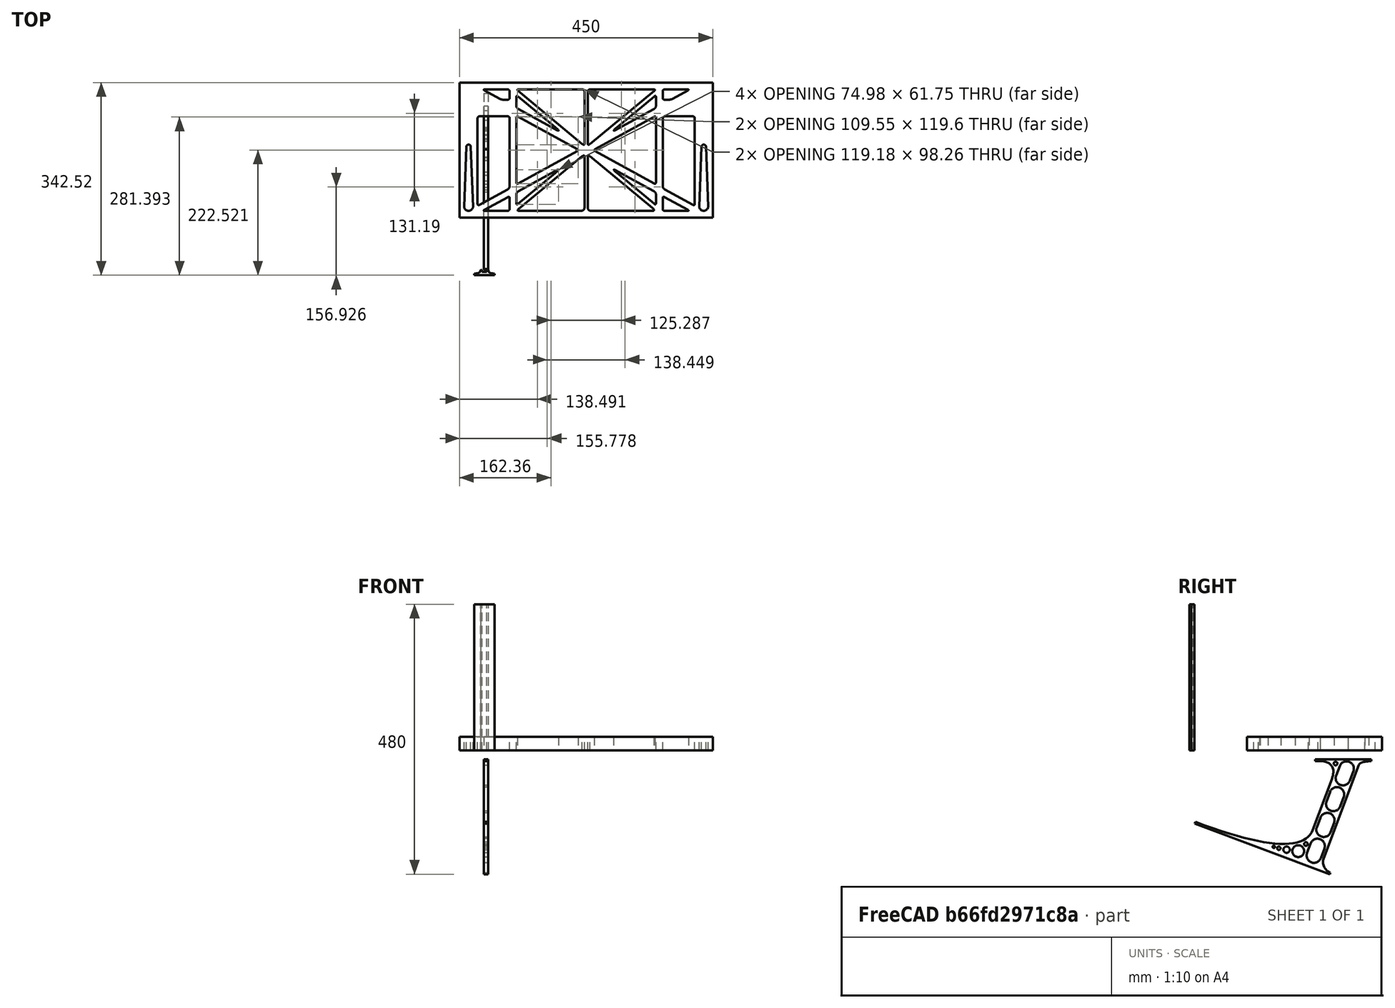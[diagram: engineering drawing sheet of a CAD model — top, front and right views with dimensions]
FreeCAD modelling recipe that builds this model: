
FCSTD DOCUMENT  (FreeCAD 0.19R0.19.2)
Label: laptopStand155FCStd
License: All rights reserved
LicenseURL: http://en.wikipedia.org/wiki/All_rights_reserved
objects: Sketcher::SketchObject×4, Part::Extrusion×3
note: 7 computed .brp shape members not serialized (recipe doc carries the construction recipe); baked Part::Feature solids carry a one-line shape summary decoded from their .brp

FEATURE [Sketcher::SketchObject] Sketch
  FullyConstrained = false
  sketch-geometry (349):
    g0: LineSegment StartX=-10.9272 StartY=-82.7794 StartZ=0 EndX=46.0728 EndY=-51.4823 EndZ=0
    g1: LineSegment StartX=-10.9272 StartY=76.4095 StartZ=0 EndX=-10.9272 EndY=-82.7794 EndZ=0
    g2: LineSegment StartX=46.0728 StartY=76.4095 StartZ=0 EndX=46.0728 EndY=-51.4823 EndZ=0
    g3: LineSegment StartX=-42.9272 StartY=136.221 StartZ=0 EndX=-42.9272 EndY=-103.779 EndZ=0
    g4: LineSegment StartX=407.073 StartY=136.221 StartZ=0 EndX=407.073 EndY=-103.779 EndZ=0
    g5: ArcOfCircle CenterX=-26.9272 CenterY=-83.7794 CenterZ=0 NormalX=0 NormalY=0 NormalZ=1 AngleXU=0 Radius=8 StartAngle=3.14159 EndAngle=6.28319
    g6: ArcOfCircle CenterX=391.073 CenterY=22.1087 CenterZ=0 NormalX=0 NormalY=0 NormalZ=1 AngleXU=0 Radius=8 StartAngle=-4.4e-15 EndAngle=3.14159
    g7: LineSegment StartX=399.073 StartY=22.1087 StartZ=0 EndX=399.073 EndY=-83.7794 EndZ=0
    g8: LineSegment StartX=383.073 StartY=22.1087 StartZ=0 EndX=383.073 EndY=-83.7794 EndZ=0
    g9: ArcOfCircle CenterX=391.073 CenterY=-83.7794 CenterZ=0 NormalX=0 NormalY=0 NormalZ=1 AngleXU=0 Radius=8 StartAngle=3.14159 EndAngle=6.28319
    g10: Circle CenterX=175.022 CenterY=27.0628 CenterZ=0 NormalX=0 NormalY=0 NormalZ=1 AngleXU=0 Radius=1
    g11: Circle CenterX=179.022 CenterY=24.8665 CenterZ=0 NormalX=0 NormalY=0 NormalZ=1 AngleXU=0 Radius=1
    g12: Circle CenterX=179.022 CenterY=27.0628 CenterZ=0 NormalX=0 NormalY=0 NormalZ=1 AngleXU=0 Radius=1
    g13: BSplineCurve PolesCount=3 KnotsCount=2 Degree=2 IsPeriodic=0
    g14: GeomPoint X=175.022 Y=27.0628 Z=0
    g15: GeomPoint X=179.022 Y=27.0628 Z=0
    g16: Circle CenterX=189.124 CenterY=27.0628 CenterZ=0 NormalX=0 NormalY=0 NormalZ=1 AngleXU=0 Radius=1
    g17: Circle CenterX=185.124 CenterY=24.8665 CenterZ=0 NormalX=0 NormalY=0 NormalZ=1 AngleXU=0 Radius=1
    g18: Circle CenterX=185.124 CenterY=27.0628 CenterZ=0 NormalX=0 NormalY=0 NormalZ=1 AngleXU=0 Radius=1
    g19: BSplineCurve PolesCount=3 KnotsCount=2 Degree=2 IsPeriodic=0
    g20: GeomPoint X=189.124 Y=27.0628 Z=0
    g21: GeomPoint X=185.124 Y=27.0628 Z=0
    g22: Circle CenterX=175.022 CenterY=5.37834 CenterZ=0 NormalX=0 NormalY=0 NormalZ=1 AngleXU=0 Radius=1
    g23: Circle CenterX=179.022 CenterY=7.57463 CenterZ=0 NormalX=0 NormalY=0 NormalZ=1 AngleXU=0 Radius=1
    g24: Circle CenterX=179.022 CenterY=5.34704 CenterZ=0 NormalX=0 NormalY=0 NormalZ=1 AngleXU=0 Radius=1
    g25: BSplineCurve PolesCount=3 KnotsCount=2 Degree=2 IsPeriodic=0
    g26: GeomPoint X=175.022 Y=5.37834 Z=0
    g27: GeomPoint X=179.022 Y=5.34704 Z=0
    g28: Circle CenterX=189.124 CenterY=5.37834 CenterZ=0 NormalX=0 NormalY=0 NormalZ=1 AngleXU=0 Radius=1
    g29: Circle CenterX=185.124 CenterY=7.57463 CenterZ=0 NormalX=0 NormalY=0 NormalZ=1 AngleXU=0 Radius=1
    g30: Circle CenterX=185.124 CenterY=5.34704 CenterZ=0 NormalX=0 NormalY=0 NormalZ=1 AngleXU=0 Radius=1
    g31: BSplineCurve PolesCount=3 KnotsCount=2 Degree=2 IsPeriodic=0
    g32: GeomPoint X=189.124 Y=5.37834 Z=0
    g33: GeomPoint X=185.124 Y=5.34704 Z=0
    g34: Circle CenterX=165.871 CenterY=18.1458 CenterZ=0 NormalX=0 NormalY=0 NormalZ=1 AngleXU=0 Radius=1
    g35: Circle CenterX=169.377 CenterY=16.2206 CenterZ=0 NormalX=0 NormalY=0 NormalZ=1 AngleXU=0 Radius=1
    g36: Circle CenterX=165.871 CenterY=14.2954 CenterZ=0 NormalX=0 NormalY=0 NormalZ=1 AngleXU=0 Radius=1
    g37: BSplineCurve PolesCount=3 KnotsCount=2 Degree=2 IsPeriodic=0
    g38: GeomPoint X=165.871 Y=18.1458 Z=0
    g39: GeomPoint X=165.871 Y=14.2954 Z=0
    g40: Circle CenterX=198.275 CenterY=18.1458 CenterZ=0 NormalX=0 NormalY=0 NormalZ=1 AngleXU=0 Radius=1
    g41: Circle CenterX=194.768 CenterY=16.2206 CenterZ=0 NormalX=0 NormalY=0 NormalZ=1 AngleXU=0 Radius=1
    g42: Circle CenterX=198.275 CenterY=14.2954 CenterZ=0 NormalX=0 NormalY=0 NormalZ=1 AngleXU=0 Radius=1
    g43: BSplineCurve PolesCount=3 KnotsCount=2 Degree=2 IsPeriodic=0
    g44: GeomPoint X=198.275 Y=18.1458 Z=0
    g45: GeomPoint X=198.275 Y=14.2954 Z=0
    g46: LineSegment StartX=407.073 StartY=-103.779 StartZ=0 EndX=-42.9272 EndY=-103.779 EndZ=0
    g47: LineSegment StartX=407.073 StartY=136.221 StartZ=0 EndX=-42.9272 EndY=136.221 EndZ=0
    g48: LineSegment StartX=46.0728 StartY=76.4095 StartZ=0 EndX=-10.9272 EndY=76.4095 EndZ=0
    g49: Circle CenterX=125.607 CenterY=54.1951 CenterZ=0 NormalX=0 NormalY=0 NormalZ=1 AngleXU=0 Radius=1
    g50: Circle CenterX=139.632 CenterY=46.4944 CenterZ=0 NormalX=0 NormalY=0 NormalZ=1 AngleXU=0 Radius=1
    g51: Circle CenterX=127.326 CenterY=56.7187 CenterZ=0 NormalX=0 NormalY=0 NormalZ=1 AngleXU=0 Radius=1
    g52: BSplineCurve PolesCount=3 KnotsCount=2 Degree=2 IsPeriodic=0
    g53: GeomPoint X=125.607 Y=54.1951 Z=0
    g54: GeomPoint X=127.326 Y=56.7187 Z=0
    g55: Circle CenterX=236.821 CenterY=56.7187 CenterZ=0 NormalX=0 NormalY=0 NormalZ=1 AngleXU=0 Radius=1
    g56: Circle CenterX=224.513 CenterY=46.4944 CenterZ=0 NormalX=0 NormalY=0 NormalZ=1 AngleXU=0 Radius=1
    g57: Circle CenterX=238.538 CenterY=54.1951 CenterZ=0 NormalX=0 NormalY=0 NormalZ=1 AngleXU=0 Radius=1
    g58: BSplineCurve PolesCount=3 KnotsCount=2 Degree=2 IsPeriodic=0
    g59: GeomPoint X=236.821 Y=56.7187 Z=0
    g60: GeomPoint X=238.538 Y=54.1951 Z=0
    g61: Circle CenterX=238.538 CenterY=-21.7539 CenterZ=0 NormalX=0 NormalY=0 NormalZ=1 AngleXU=0 Radius=1
    g62: Circle CenterX=224.513 CenterY=-14.0532 CenterZ=0 NormalX=0 NormalY=0 NormalZ=1 AngleXU=0 Radius=1
    g63: Circle CenterX=236.821 CenterY=-24.2775 CenterZ=0 NormalX=0 NormalY=0 NormalZ=1 AngleXU=0 Radius=1
    g64: BSplineCurve PolesCount=3 KnotsCount=2 Degree=2 IsPeriodic=0
    g65: GeomPoint X=238.538 Y=-21.7539 Z=0
    g66: GeomPoint X=236.821 Y=-24.2775 Z=0
    g67: Circle CenterX=125.607 CenterY=-21.7539 CenterZ=0 NormalX=0 NormalY=0 NormalZ=1 AngleXU=0 Radius=1
    g68: Circle CenterX=139.632 CenterY=-14.0532 CenterZ=0 NormalX=0 NormalY=0 NormalZ=1 AngleXU=0 Radius=1
    g69: Circle CenterX=127.325 CenterY=-24.2775 CenterZ=0 NormalX=0 NormalY=0 NormalZ=1 AngleXU=0 Radius=1
    g70: BSplineCurve PolesCount=3 KnotsCount=2 Degree=2 IsPeriodic=0
    g71: GeomPoint X=125.607 Y=-21.7539 Z=0
    g72: GeomPoint X=127.325 Y=-24.2775 Z=0
    g73: Circle CenterX=302.996 CenterY=111.695 CenterZ=0 NormalX=0 NormalY=0 NormalZ=1 AngleXU=0 Radius=1
    g74: Circle CenterX=306.073 CenterY=114.251 CenterZ=0 NormalX=0 NormalY=0 NormalZ=1 AngleXU=0 Radius=1
    g75: Circle CenterX=306.073 CenterY=110.251 CenterZ=0 NormalX=0 NormalY=0 NormalZ=1 AngleXU=0 Radius=1
    g76: BSplineCurve PolesCount=3 KnotsCount=2 Degree=2 IsPeriodic=0
    g77: GeomPoint X=302.996 Y=111.695 Z=0
    g78: GeomPoint X=306.073 Y=110.251 Z=0
    g79: Circle CenterX=306.073 CenterY=95.2763 CenterZ=0 NormalX=0 NormalY=0 NormalZ=1 AngleXU=0 Radius=1
    g80: Circle CenterX=306.073 CenterY=91.2763 CenterZ=0 NormalX=0 NormalY=0 NormalZ=1 AngleXU=0 Radius=1
    g81: Circle CenterX=302.567 CenterY=89.3511 CenterZ=0 NormalX=0 NormalY=0 NormalZ=1 AngleXU=0 Radius=1
    g82: BSplineCurve PolesCount=3 KnotsCount=2 Degree=2 IsPeriodic=0
    g83: GeomPoint X=306.073 Y=95.2763 Z=0
    g84: GeomPoint X=302.567 Y=89.3511 Z=0
    g85: LineSegment StartX=306.073 StartY=110.251 StartZ=0 EndX=306.073 EndY=95.2763 EndZ=0
    g86: LineSegment StartX=302.996 StartY=111.695 StartZ=0 EndX=236.821 EndY=56.7187 EndZ=0
    g87: LineSegment StartX=238.538 StartY=54.1951 StartZ=0 EndX=302.567 EndY=89.3511 EndZ=0
    g88: Circle CenterX=61.1496 CenterY=111.695 CenterZ=0 NormalX=0 NormalY=0 NormalZ=1 AngleXU=0 Radius=1
    g89: Circle CenterX=58.0728 CenterY=114.251 CenterZ=0 NormalX=0 NormalY=0 NormalZ=1 AngleXU=0 Radius=1
    g90: Circle CenterX=58.0728 CenterY=110.251 CenterZ=0 NormalX=0 NormalY=0 NormalZ=1 AngleXU=0 Radius=1
    g91: BSplineCurve PolesCount=3 KnotsCount=2 Degree=2 IsPeriodic=0
    g92: GeomPoint X=61.1496 Y=111.695 Z=0
    g93: GeomPoint X=58.0728 Y=110.251 Z=0
    g94: Circle CenterX=61.5791 CenterY=89.3511 CenterZ=0 NormalX=0 NormalY=0 NormalZ=1 AngleXU=0 Radius=1
    g95: Circle CenterX=58.0728 CenterY=91.2763 CenterZ=0 NormalX=0 NormalY=0 NormalZ=1 AngleXU=0 Radius=1
    g96: Circle CenterX=58.0728 CenterY=95.2763 CenterZ=0 NormalX=0 NormalY=0 NormalZ=1 AngleXU=0 Radius=1
    g97: BSplineCurve PolesCount=3 KnotsCount=2 Degree=2 IsPeriodic=0
    g98: GeomPoint X=61.5791 Y=89.3511 Z=0
    g99: GeomPoint X=58.0728 Y=95.2763 Z=0
    g100: LineSegment StartX=58.0728 StartY=110.251 StartZ=0 EndX=58.0728 EndY=95.2763 EndZ=0
    g101: LineSegment StartX=61.1496 StartY=111.695 StartZ=0 EndX=127.326 EndY=56.7187 EndZ=0
    g102: LineSegment StartX=125.607 StartY=54.1951 StartZ=0 EndX=61.5791 EndY=89.3511 EndZ=0
    g103: Circle CenterX=61.5791 CenterY=-56.9099 CenterZ=0 NormalX=0 NormalY=0 NormalZ=1 AngleXU=0 Radius=1
    g104: Circle CenterX=58.0728 CenterY=-58.8351 CenterZ=0 NormalX=0 NormalY=0 NormalZ=1 AngleXU=0 Radius=1
    g105: Circle CenterX=58.0728 CenterY=-62.8351 CenterZ=0 NormalX=0 NormalY=0 NormalZ=1 AngleXU=0 Radius=1
    g106: BSplineCurve PolesCount=3 KnotsCount=2 Degree=2 IsPeriodic=0
    g107: GeomPoint X=61.5791 Y=-56.9099 Z=0
    g108: GeomPoint X=58.0728 Y=-62.8351 Z=0
    g109: Circle CenterX=58.0728 CenterY=-77.8102 CenterZ=0 NormalX=0 NormalY=0 NormalZ=1 AngleXU=0 Radius=1
    g110: Circle CenterX=58.0728 CenterY=-81.8102 CenterZ=0 NormalX=0 NormalY=0 NormalZ=1 AngleXU=0 Radius=1
    g111: Circle CenterX=61.1496 CenterY=-79.2541 CenterZ=0 NormalX=0 NormalY=0 NormalZ=1 AngleXU=0 Radius=1
    g112: BSplineCurve PolesCount=3 KnotsCount=2 Degree=2 IsPeriodic=0
    g113: GeomPoint X=58.0728 Y=-77.8102 Z=0
    g114: GeomPoint X=61.1496 Y=-79.2541 Z=0
    g115: LineSegment StartX=58.0728 StartY=-62.8351 StartZ=0 EndX=58.0728 EndY=-77.8102 EndZ=0
    g116: LineSegment StartX=61.1496 StartY=-79.2541 StartZ=0 EndX=127.325 EndY=-24.2775 EndZ=0
    g117: LineSegment StartX=125.607 StartY=-21.7539 StartZ=0 EndX=61.5791 EndY=-56.9099 EndZ=0
    g118: Circle CenterX=302.567 CenterY=-56.9099 CenterZ=0 NormalX=0 NormalY=0 NormalZ=1 AngleXU=0 Radius=1
    g119: Circle CenterX=306.073 CenterY=-58.8351 CenterZ=0 NormalX=0 NormalY=0 NormalZ=1 AngleXU=0 Radius=1
    g120: Circle CenterX=306.073 CenterY=-62.8351 CenterZ=0 NormalX=0 NormalY=0 NormalZ=1 AngleXU=0 Radius=1
    g121: BSplineCurve PolesCount=3 KnotsCount=2 Degree=2 IsPeriodic=0
    g122: GeomPoint X=302.567 Y=-56.9099 Z=0
    g123: GeomPoint X=306.073 Y=-62.8351 Z=0
    g124: Circle CenterX=302.996 CenterY=-79.2541 CenterZ=0 NormalX=0 NormalY=0 NormalZ=1 AngleXU=0 Radius=1
    g125: Circle CenterX=306.073 CenterY=-81.8102 CenterZ=0 NormalX=0 NormalY=0 NormalZ=1 AngleXU=0 Radius=1
    g126: Circle CenterX=306.073 CenterY=-77.8102 CenterZ=0 NormalX=0 NormalY=0 NormalZ=1 AngleXU=0 Radius=1
    g127: BSplineCurve PolesCount=3 KnotsCount=2 Degree=2 IsPeriodic=0
    g128: GeomPoint X=302.996 Y=-79.2541 Z=0
    g129: GeomPoint X=306.073 Y=-77.8102 Z=0
    g130: LineSegment StartX=306.073 StartY=-62.8351 StartZ=0 EndX=306.073 EndY=-77.8102 EndZ=0
    g131: LineSegment StartX=302.996 StartY=-79.2541 StartZ=0 EndX=236.821 EndY=-24.2775 EndZ=0
    g132: LineSegment StartX=238.538 StartY=-21.7539 StartZ=0 EndX=302.567 EndY=-56.9099 EndZ=0
    g133: Circle CenterX=61.6457 CenterY=-88.8112 CenterZ=0 NormalX=0 NormalY=0 NormalZ=1 AngleXU=0 Radius=1
    g134: Circle CenterX=58.0728 CenterY=-91.7794 CenterZ=0 NormalX=0 NormalY=0 NormalZ=1 AngleXU=0 Radius=1
    g135: Circle CenterX=63.9135 CenterY=-91.7794 CenterZ=0 NormalX=0 NormalY=0 NormalZ=1 AngleXU=0 Radius=1
    g136: BSplineCurve PolesCount=3 KnotsCount=2 Degree=2 IsPeriodic=0
    g137: GeomPoint X=61.6457 Y=-88.8112 Z=0
    g138: GeomPoint X=63.9135 Y=-91.7794 Z=0
    g139: Circle CenterX=179.022 CenterY=-85.8163 CenterZ=0 NormalX=0 NormalY=0 NormalZ=1 AngleXU=0 Radius=1
    g140: Circle CenterX=179.022 CenterY=-91.7794 CenterZ=0 NormalX=0 NormalY=0 NormalZ=1 AngleXU=0 Radius=1
    g141: Circle CenterX=171.895 CenterY=-91.7794 CenterZ=0 NormalX=0 NormalY=0 NormalZ=1 AngleXU=0 Radius=1
    g142: BSplineCurve PolesCount=3 KnotsCount=2 Degree=2 IsPeriodic=0
    g143: GeomPoint X=179.022 Y=-85.8163 Z=0
    g144: GeomPoint X=171.895 Y=-91.7794 Z=0
    g145: Circle CenterX=185.124 CenterY=-86.2028 CenterZ=0 NormalX=0 NormalY=0 NormalZ=1 AngleXU=0 Radius=1
    g146: Circle CenterX=185.124 CenterY=-91.7794 CenterZ=0 NormalX=0 NormalY=0 NormalZ=1 AngleXU=0 Radius=1
    g147: Circle CenterX=191.747 CenterY=-91.7794 CenterZ=0 NormalX=0 NormalY=0 NormalZ=1 AngleXU=0 Radius=1
    g148: BSplineCurve PolesCount=3 KnotsCount=2 Degree=2 IsPeriodic=0
    g149: GeomPoint X=185.124 Y=-86.2028 Z=0
    g150: GeomPoint X=191.747 Y=-91.7794 Z=0
    g151: Circle CenterX=299.888 CenterY=-86.6413 CenterZ=0 NormalX=0 NormalY=0 NormalZ=1 AngleXU=0 Radius=1
    g152: Circle CenterX=306.073 CenterY=-91.7794 CenterZ=0 NormalX=0 NormalY=0 NormalZ=1 AngleXU=0 Radius=1
    g153: Circle CenterX=298.776 CenterY=-91.7794 CenterZ=0 NormalX=0 NormalY=0 NormalZ=1 AngleXU=0 Radius=1
    g154: BSplineCurve PolesCount=3 KnotsCount=2 Degree=2 IsPeriodic=0
    g155: GeomPoint X=299.888 Y=-86.6413 Z=0
    g156: GeomPoint X=298.776 Y=-91.7794 Z=0
    g157: LineSegment StartX=189.124 StartY=5.37834 StartZ=0 EndX=299.888 EndY=-86.6413 EndZ=0
    g158: LineSegment StartX=298.776 StartY=-91.7794 StartZ=0 EndX=191.747 EndY=-91.7794 EndZ=0
    g159: LineSegment StartX=185.124 StartY=-86.2028 StartZ=0 EndX=185.124 EndY=5.34704 EndZ=0
    g160: LineSegment StartX=179.022 StartY=5.34704 StartZ=0 EndX=179.022 EndY=-85.8163 EndZ=0
    g161: LineSegment StartX=171.895 StartY=-91.7794 StartZ=0 EndX=63.9135 EndY=-91.7794 EndZ=0
    g162: LineSegment StartX=61.6457 StartY=-88.8112 StartZ=0 EndX=175.022 EndY=5.37834 EndZ=0
    g163: Circle CenterX=302.073 CenterY=124.221 CenterZ=0 NormalX=0 NormalY=0 NormalZ=1 AngleXU=0 Radius=1
    g164: Circle CenterX=306.073 CenterY=124.221 CenterZ=0 NormalX=0 NormalY=0 NormalZ=1 AngleXU=0 Radius=1
    g165: Circle CenterX=302.996 CenterY=121.665 CenterZ=0 NormalX=0 NormalY=0 NormalZ=1 AngleXU=0 Radius=1
    g166: BSplineCurve PolesCount=3 KnotsCount=2 Degree=2 IsPeriodic=0
    g167: GeomPoint X=302.073 Y=124.221 Z=0
    g168: GeomPoint X=302.996 Y=121.665 Z=0
    g169: Circle CenterX=189.124 CenterY=124.221 CenterZ=0 NormalX=0 NormalY=0 NormalZ=1 AngleXU=0 Radius=1
    g170: Circle CenterX=185.124 CenterY=124.221 CenterZ=0 NormalX=0 NormalY=0 NormalZ=1 AngleXU=0 Radius=1
    g171: Circle CenterX=185.124 CenterY=120.221 CenterZ=0 NormalX=0 NormalY=0 NormalZ=1 AngleXU=0 Radius=1
    g172: BSplineCurve PolesCount=3 KnotsCount=2 Degree=2 IsPeriodic=0
    g173: GeomPoint X=189.124 Y=124.221 Z=0
    g174: GeomPoint X=185.124 Y=120.221 Z=0
    g175: Circle CenterX=175.022 CenterY=124.221 CenterZ=0 NormalX=0 NormalY=0 NormalZ=1 AngleXU=0 Radius=1
    g176: Circle CenterX=179.022 CenterY=124.221 CenterZ=0 NormalX=0 NormalY=0 NormalZ=1 AngleXU=0 Radius=1
    g177: Circle CenterX=179.022 CenterY=120.221 CenterZ=0 NormalX=0 NormalY=0 NormalZ=1 AngleXU=0 Radius=1
    g178: BSplineCurve PolesCount=3 KnotsCount=2 Degree=2 IsPeriodic=0
    g179: GeomPoint X=175.022 Y=124.221 Z=0
    g180: GeomPoint X=179.022 Y=120.221 Z=0
    g181: Circle CenterX=62.0728 CenterY=124.221 CenterZ=0 NormalX=0 NormalY=0 NormalZ=1 AngleXU=0 Radius=1
    g182: Circle CenterX=58.0728 CenterY=124.221 CenterZ=0 NormalX=0 NormalY=0 NormalZ=1 AngleXU=0 Radius=1
    g183: Circle CenterX=61.1496 CenterY=121.665 CenterZ=0 NormalX=0 NormalY=0 NormalZ=1 AngleXU=0 Radius=1
    g184: BSplineCurve PolesCount=3 KnotsCount=2 Degree=2 IsPeriodic=0
    g185: GeomPoint X=62.0728 Y=124.221 Z=0
    g186: GeomPoint X=61.1496 Y=121.665 Z=0
    g187: LineSegment StartX=62.0728 StartY=124.221 StartZ=0 EndX=175.022 EndY=124.221 EndZ=0
    g188: LineSegment StartX=179.022 StartY=120.221 StartZ=0 EndX=179.022 EndY=27.0628 EndZ=0
    g189: LineSegment StartX=185.124 StartY=27.0628 StartZ=0 EndX=185.124 EndY=120.221 EndZ=0
    g190: LineSegment StartX=189.124 StartY=124.221 StartZ=0 EndX=302.073 EndY=124.221 EndZ=0
    g191: LineSegment StartX=302.996 StartY=121.665 StartZ=0 EndX=189.124 EndY=27.0628 EndZ=0
    g192: LineSegment StartX=175.022 StartY=27.0628 StartZ=0 EndX=61.1496 EndY=121.665 EndZ=0
    g193: Circle CenterX=61.5791 CenterY=75.4095 CenterZ=0 NormalX=0 NormalY=0 NormalZ=1 AngleXU=0 Radius=1
    g194: Circle CenterX=58.0728 CenterY=77.3346 CenterZ=0 NormalX=0 NormalY=0 NormalZ=1 AngleXU=0 Radius=1
    g195: Circle CenterX=58.0728 CenterY=73.3346 CenterZ=0 NormalX=0 NormalY=0 NormalZ=1 AngleXU=0 Radius=1
    g196: BSplineCurve PolesCount=3 KnotsCount=2 Degree=2 IsPeriodic=0
    g197: GeomPoint X=61.5791 Y=75.4095 Z=0
    g198: GeomPoint X=58.0728 Y=73.3346 Z=0
    g199: Circle CenterX=58.0728 CenterY=-40.8935 CenterZ=0 NormalX=0 NormalY=0 NormalZ=1 AngleXU=0 Radius=1
    g200: Circle CenterX=58.0728 CenterY=-44.8935 CenterZ=0 NormalX=0 NormalY=0 NormalZ=1 AngleXU=0 Radius=1
    g201: Circle CenterX=61.5791 CenterY=-42.9683 CenterZ=0 NormalX=0 NormalY=0 NormalZ=1 AngleXU=0 Radius=1
    g202: BSplineCurve PolesCount=3 KnotsCount=2 Degree=2 IsPeriodic=0
    g203: GeomPoint X=58.0728 Y=-40.8935 Z=0
    g204: GeomPoint X=61.5791 Y=-42.9683 Z=0
    g205: LineSegment StartX=61.5791 StartY=-42.9683 StartZ=0 EndX=165.871 EndY=14.2954 EndZ=0
    g206: LineSegment StartX=165.871 StartY=18.1458 StartZ=0 EndX=61.5791 EndY=75.4095 EndZ=0
    g207: LineSegment StartX=58.0728 StartY=73.3346 StartZ=0 EndX=58.0728 EndY=-40.8935 EndZ=0
    g208: Circle CenterX=302.567 CenterY=-42.9683 CenterZ=0 NormalX=0 NormalY=0 NormalZ=1 AngleXU=0 Radius=1
    g209: Circle CenterX=306.073 CenterY=-44.8935 CenterZ=0 NormalX=0 NormalY=0 NormalZ=1 AngleXU=0 Radius=1
    g210: Circle CenterX=306.073 CenterY=-40.8935 CenterZ=0 NormalX=0 NormalY=0 NormalZ=1 AngleXU=0 Radius=1
    g211: BSplineCurve PolesCount=3 KnotsCount=2 Degree=2 IsPeriodic=0
    g212: GeomPoint X=302.567 Y=-42.9683 Z=0
    g213: GeomPoint X=306.073 Y=-40.8935 Z=0
    g214: Circle CenterX=306.073 CenterY=73.3346 CenterZ=0 NormalX=0 NormalY=0 NormalZ=1 AngleXU=0 Radius=1
    g215: Circle CenterX=306.073 CenterY=77.3346 CenterZ=0 NormalX=0 NormalY=0 NormalZ=1 AngleXU=0 Radius=1
    g216: Circle CenterX=302.567 CenterY=75.4095 CenterZ=0 NormalX=0 NormalY=0 NormalZ=1 AngleXU=0 Radius=1
    g217: BSplineCurve PolesCount=3 KnotsCount=2 Degree=2 IsPeriodic=0
    g218: GeomPoint X=306.073 Y=73.3346 Z=0
    g219: GeomPoint X=302.567 Y=75.4095 Z=0
    g220: LineSegment StartX=302.567 StartY=-42.9683 StartZ=0 EndX=198.275 EndY=14.2954 EndZ=0
    g221: LineSegment StartX=198.275 StartY=18.1458 StartZ=0 EndX=302.567 EndY=75.4095 EndZ=0
    g222: LineSegment StartX=306.073 StartY=73.3346 StartZ=0 EndX=306.073 EndY=-40.8935 EndZ=0
    g223: LineSegment StartX=322.073 StartY=105.865 StartZ=0 EndX=328.643 EndY=105.865 EndZ=0
    g224: LineSegment StartX=318.073 StartY=120.221 StartZ=0 EndX=318.073 EndY=109.865 EndZ=0
    g225: LineSegment StartX=336.157 StartY=107.779 StartZ=0 EndX=362.567 EndY=122.294 EndZ=0
    g226: Circle CenterX=362.073 CenterY=124.221 CenterZ=0 NormalX=0 NormalY=0 NormalZ=1 AngleXU=0 Radius=1
    g227: Circle CenterX=366.073 CenterY=124.221 CenterZ=0 NormalX=0 NormalY=0 NormalZ=1 AngleXU=0 Radius=1
    g228: Circle CenterX=362.567 CenterY=122.294 CenterZ=0 NormalX=0 NormalY=0 NormalZ=1 AngleXU=0 Radius=1
    g229: BSplineCurve PolesCount=3 KnotsCount=2 Degree=2 IsPeriodic=0
    g230: GeomPoint X=362.073 Y=124.221 Z=0
    g231: GeomPoint X=362.567 Y=122.294 Z=0
    g232: Circle CenterX=322.073 CenterY=124.221 CenterZ=0 NormalX=0 NormalY=0 NormalZ=1 AngleXU=0 Radius=1
    g233: Circle CenterX=318.073 CenterY=124.221 CenterZ=0 NormalX=0 NormalY=0 NormalZ=1 AngleXU=0 Radius=1
    g234: Circle CenterX=318.073 CenterY=120.221 CenterZ=0 NormalX=0 NormalY=0 NormalZ=1 AngleXU=0 Radius=1
    g235: BSplineCurve PolesCount=3 KnotsCount=2 Degree=2 IsPeriodic=0
    g236: GeomPoint X=322.073 Y=124.221 Z=0
    g237: GeomPoint X=318.073 Y=120.221 Z=0
    g238: Circle CenterX=322.073 CenterY=105.865 CenterZ=0 NormalX=0 NormalY=0 NormalZ=1 AngleXU=0 Radius=1
    g239: Circle CenterX=318.073 CenterY=105.865 CenterZ=0 NormalX=0 NormalY=0 NormalZ=1 AngleXU=0 Radius=1
    g240: Circle CenterX=318.073 CenterY=109.865 CenterZ=0 NormalX=0 NormalY=0 NormalZ=1 AngleXU=0 Radius=1
    g241: BSplineCurve PolesCount=3 KnotsCount=2 Degree=2 IsPeriodic=0
    g242: GeomPoint X=322.073 Y=105.865 Z=0
    g243: GeomPoint X=318.073 Y=109.865 Z=0
    g244: Circle CenterX=336.157 CenterY=107.779 CenterZ=0 NormalX=0 NormalY=0 NormalZ=1 AngleXU=0 Radius=1
    g245: Circle CenterX=332.651 CenterY=105.853 CenterZ=0 NormalX=0 NormalY=0 NormalZ=1 AngleXU=0 Radius=1
    g246: Circle CenterX=328.643 CenterY=105.865 CenterZ=0 NormalX=0 NormalY=0 NormalZ=1 AngleXU=0 Radius=1
    g247: BSplineCurve PolesCount=3 KnotsCount=2 Degree=2 IsPeriodic=0
    g248: GeomPoint X=336.157 Y=107.779 Z=0
    g249: GeomPoint X=328.643 Y=105.865 Z=0
    g250: LineSegment StartX=322.073 StartY=124.221 StartZ=0 EndX=362.073 EndY=124.221 EndZ=0
    g251: Circle CenterX=371.567 CenterY=-80.8644 CenterZ=0 NormalX=0 NormalY=0 NormalZ=1 AngleXU=0 Radius=1
    g252: Circle CenterX=375.073 CenterY=-82.7896 CenterZ=0 NormalX=0 NormalY=0 NormalZ=1 AngleXU=0 Radius=1
    g253: Circle CenterX=375.073 CenterY=-78.7896 CenterZ=0 NormalX=0 NormalY=0 NormalZ=1 AngleXU=0 Radius=1
    g254: BSplineCurve PolesCount=3 KnotsCount=2 Degree=2 IsPeriodic=0
    g255: GeomPoint X=371.567 Y=-80.8644 Z=0
    g256: GeomPoint X=375.073 Y=-78.7896 Z=0
    g257: Circle CenterX=321.579 CenterY=-53.4075 CenterZ=0 NormalX=0 NormalY=0 NormalZ=1 AngleXU=0 Radius=1
    g258: Circle CenterX=318.073 CenterY=-51.4823 CenterZ=0 NormalX=0 NormalY=0 NormalZ=1 AngleXU=0 Radius=1
    g259: Circle CenterX=318.073 CenterY=-47.4805 CenterZ=0 NormalX=0 NormalY=0 NormalZ=1 AngleXU=0 Radius=1
    g260: BSplineCurve PolesCount=3 KnotsCount=2 Degree=2 IsPeriodic=0
    g261: GeomPoint X=321.579 Y=-53.4075 Z=0
    g262: GeomPoint X=318.073 Y=-47.4805 Z=0
    g263: LineSegment StartX=371.567 StartY=-80.8644 StartZ=0 EndX=321.579 EndY=-53.4075 EndZ=0
    g264: Circle CenterX=321.579 CenterY=-67.3492 CenterZ=0 NormalX=0 NormalY=0 NormalZ=1 AngleXU=0 Radius=1
    g265: Circle CenterX=318.073 CenterY=-65.424 CenterZ=0 NormalX=0 NormalY=0 NormalZ=1 AngleXU=0 Radius=1
    g266: Circle CenterX=318.073 CenterY=-69.424 CenterZ=0 NormalX=0 NormalY=0 NormalZ=1 AngleXU=0 Radius=1
    g267: BSplineCurve PolesCount=3 KnotsCount=2 Degree=2 IsPeriodic=0
    g268: GeomPoint X=321.579 Y=-67.3492 Z=0
    g269: GeomPoint X=318.073 Y=-69.424 Z=0
    g270: Circle CenterX=362.567 CenterY=-89.8542 CenterZ=0 NormalX=0 NormalY=0 NormalZ=1 AngleXU=0 Radius=1
    g271: Circle CenterX=366.073 CenterY=-91.7794 CenterZ=0 NormalX=0 NormalY=0 NormalZ=1 AngleXU=0 Radius=1
    g272: Circle CenterX=362.073 CenterY=-91.7794 CenterZ=0 NormalX=0 NormalY=0 NormalZ=1 AngleXU=0 Radius=1
    g273: BSplineCurve PolesCount=3 KnotsCount=2 Degree=2 IsPeriodic=0
    g274: GeomPoint X=362.567 Y=-89.8542 Z=0
    g275: GeomPoint X=362.073 Y=-91.7794 Z=0
    g276: Circle CenterX=322.073 CenterY=-91.7794 CenterZ=0 NormalX=0 NormalY=0 NormalZ=1 AngleXU=0 Radius=1
    g277: Circle CenterX=318.073 CenterY=-91.7794 CenterZ=0 NormalX=0 NormalY=0 NormalZ=1 AngleXU=0 Radius=1
    g278: Circle CenterX=318.073 CenterY=-87.7794 CenterZ=0 NormalX=0 NormalY=0 NormalZ=1 AngleXU=0 Radius=1
    g279: BSplineCurve PolesCount=3 KnotsCount=2 Degree=2 IsPeriodic=0
    g280: GeomPoint X=322.073 Y=-91.7794 Z=0
    g281: GeomPoint X=318.073 Y=-87.7794 Z=0
    g282: LineSegment StartX=362.567 StartY=-89.8542 StartZ=0 EndX=321.579 EndY=-67.3492 EndZ=0
    g283: LineSegment StartX=318.073 StartY=-69.424 StartZ=0 EndX=318.073 EndY=-87.7794 EndZ=0
    g284: LineSegment StartX=322.073 StartY=-91.7794 StartZ=0 EndX=362.073 EndY=-91.7794 EndZ=0
    g285: Circle CenterX=2.07281 CenterY=124.221 CenterZ=0 NormalX=0 NormalY=0 NormalZ=1 AngleXU=0 Radius=1
    g286: Circle CenterX=1.57905 CenterY=122.295 CenterZ=0 NormalX=0 NormalY=0 NormalZ=1 AngleXU=0 Radius=1
    g287: BSplineCurve PolesCount=3 KnotsCount=2 Degree=2 IsPeriodic=0
    g288: GeomPoint X=2.07281 Y=124.221 Z=0
    g289: GeomPoint X=1.57905 Y=122.295 Z=0
    g290: Circle CenterX=42.0728 CenterY=124.221 CenterZ=0 NormalX=0 NormalY=0 NormalZ=1 AngleXU=0 Radius=1
    g291: Circle CenterX=46.0728 CenterY=124.221 CenterZ=0 NormalX=0 NormalY=0 NormalZ=1 AngleXU=0 Radius=1
    g292: Circle CenterX=46.0728 CenterY=120.221 CenterZ=0 NormalX=0 NormalY=0 NormalZ=1 AngleXU=0 Radius=1
    g293: BSplineCurve PolesCount=3 KnotsCount=2 Degree=2 IsPeriodic=0
    g294: GeomPoint X=42.0728 Y=124.221 Z=0
    g295: GeomPoint X=46.0728 Y=120.221 Z=0
    g296: Circle CenterX=46.0728 CenterY=109.865 CenterZ=0 NormalX=0 NormalY=0 NormalZ=1 AngleXU=0 Radius=1
    g297: Circle CenterX=46.0728 CenterY=105.865 CenterZ=0 NormalX=0 NormalY=0 NormalZ=1 AngleXU=0 Radius=1
    g298: Circle CenterX=42.0728 CenterY=105.865 CenterZ=0 NormalX=0 NormalY=0 NormalZ=1 AngleXU=0 Radius=1
    g299: BSplineCurve PolesCount=3 KnotsCount=2 Degree=2 IsPeriodic=0
    g300: GeomPoint X=46.0728 Y=109.865 Z=0
    g301: GeomPoint X=42.0728 Y=105.865 Z=0
    g302: Circle CenterX=35.5028 CenterY=105.865 CenterZ=0 NormalX=0 NormalY=0 NormalZ=1 AngleXU=0 Radius=1
    g303: Circle CenterX=31.5028 CenterY=105.865 CenterZ=0 NormalX=0 NormalY=0 NormalZ=1 AngleXU=0 Radius=1
    g304: Circle CenterX=27.9965 CenterY=107.79 CenterZ=0 NormalX=0 NormalY=0 NormalZ=1 AngleXU=0 Radius=1
    g305: BSplineCurve PolesCount=3 KnotsCount=2 Degree=2 IsPeriodic=0
    g306: GeomPoint X=35.5028 Y=105.865 Z=0
    g307: GeomPoint X=27.9965 Y=107.79 Z=0
    g308: LineSegment StartX=2.07281 StartY=124.221 StartZ=0 EndX=42.0728 EndY=124.221 EndZ=0
    g309: LineSegment StartX=46.0728 StartY=120.221 StartZ=0 EndX=46.0728 EndY=109.865 EndZ=0
    g310: LineSegment StartX=42.0728 StartY=105.865 StartZ=0 EndX=35.5028 EndY=105.865 EndZ=0
    g311: LineSegment StartX=27.9965 StartY=107.79 StartZ=0 EndX=1.57905 EndY=122.295 EndZ=0
    g312: Circle CenterX=42.5666 CenterY=-67.3492 CenterZ=0 NormalX=0 NormalY=0 NormalZ=1 AngleXU=0 Radius=1
    g313: Circle CenterX=46.0728 CenterY=-65.424 CenterZ=0 NormalX=0 NormalY=0 NormalZ=1 AngleXU=0 Radius=1
    g314: Circle CenterX=46.0728 CenterY=-69.424 CenterZ=0 NormalX=0 NormalY=0 NormalZ=1 AngleXU=0 Radius=1
    g315: BSplineCurve PolesCount=3 KnotsCount=2 Degree=2 IsPeriodic=0
    g316: GeomPoint X=42.5666 Y=-67.3492 Z=0
    g317: GeomPoint X=46.0728 Y=-69.424 Z=0
    g318: Circle CenterX=46.0728 CenterY=-87.7794 CenterZ=0 NormalX=0 NormalY=0 NormalZ=1 AngleXU=0 Radius=1
    g319: Circle CenterX=46.0728 CenterY=-91.7794 CenterZ=0 NormalX=0 NormalY=0 NormalZ=1 AngleXU=0 Radius=1
    g320: Circle CenterX=42.0728 CenterY=-91.7794 CenterZ=0 NormalX=0 NormalY=0 NormalZ=1 AngleXU=0 Radius=1
    g321: BSplineCurve PolesCount=3 KnotsCount=2 Degree=2 IsPeriodic=0
    g322: GeomPoint X=46.0728 Y=-87.7794 Z=0
    g323: GeomPoint X=42.0728 Y=-91.7794 Z=0
    g324: Circle CenterX=2.07281 CenterY=-91.7794 CenterZ=0 NormalX=0 NormalY=0 NormalZ=1 AngleXU=0 Radius=1
    g325: Circle CenterX=-1.92719 CenterY=-91.7794 CenterZ=0 NormalX=0 NormalY=0 NormalZ=1 AngleXU=0 Radius=1
    g326: Circle CenterX=1.57905 CenterY=-89.8542 CenterZ=0 NormalX=0 NormalY=0 NormalZ=1 AngleXU=0 Radius=1
    g327: BSplineCurve PolesCount=3 KnotsCount=2 Degree=2 IsPeriodic=0
    g328: GeomPoint X=2.07281 Y=-91.7794 Z=0
    g329: GeomPoint X=1.57905 Y=-89.8542 Z=0
    g330: LineSegment StartX=2.07281 StartY=-91.7794 StartZ=0 EndX=42.0728 EndY=-91.7794 EndZ=0
    g331: LineSegment StartX=46.0728 StartY=-87.7794 StartZ=0 EndX=46.0728 EndY=-69.424 EndZ=0
    g332: LineSegment StartX=42.5666 StartY=-67.3492 StartZ=0 EndX=1.57905 EndY=-89.8542 EndZ=0
    g333: Circle CenterX=322.073 CenterY=76.4095 CenterZ=0 NormalX=0 NormalY=0 NormalZ=1 AngleXU=0 Radius=4
    g334: BSplineCurve PolesCount=3 KnotsCount=2 Degree=2 IsPeriodic=0
    g335: GeomPoint X=318.073 Y=72.4095 Z=0
    g336: GeomPoint X=322.073 Y=76.4095 Z=0
    g337: Circle CenterX=375.073 CenterY=72.4095 CenterZ=0 NormalX=0 NormalY=0 NormalZ=1 AngleXU=0 Radius=1
    g338: Circle CenterX=375.073 CenterY=76.4095 CenterZ=0 NormalX=0 NormalY=0 NormalZ=1 AngleXU=0 Radius=1
    g339: Circle CenterX=371.073 CenterY=76.4095 CenterZ=0 NormalX=0 NormalY=0 NormalZ=1 AngleXU=0 Radius=1
    g340: BSplineCurve PolesCount=3 KnotsCount=2 Degree=2 IsPeriodic=0
    g341: GeomPoint X=375.073 Y=72.4095 Z=0
    g342: GeomPoint X=371.073 Y=76.4095 Z=0
    g343: LineSegment StartX=322.073 StartY=76.4095 StartZ=0 EndX=371.073 EndY=76.4095 EndZ=0
    g344: LineSegment StartX=318.073 StartY=72.4095 StartZ=0 EndX=318.073 EndY=-47.4805 EndZ=0
    g345: LineSegment StartX=375.073 StartY=72.4095 StartZ=0 EndX=375.073 EndY=-78.7896 EndZ=0
    g346: ArcOfCircle CenterX=-26.9272 CenterY=22.1087 CenterZ=0 NormalX=0 NormalY=0 NormalZ=1 AngleXU=0 Radius=4 StartAngle=5e-16 EndAngle=3.14159
    g347: LineSegment StartX=-30.9272 StartY=22.1087 StartZ=0 EndX=-34.9272 EndY=-83.7794 EndZ=0
    g348: LineSegment StartX=-18.9272 StartY=-83.7794 StartZ=0 EndX=-22.9272 EndY=22.1087 EndZ=0
  constraints (572):
    c: Coincident(g0,g2)
    c: Block(g0)
    c: Block(g1)
    c: Vertical(g3)
    c: Vertical(g4)
    c: Block(g4)
    c: Block(g3)
    c: Tangent(g6,g7) = 1.5708
    c: Tangent(g7,g9) = 1.5708
    c: Equal(g6,g9)
    c: Coincident(g8,g6)
    c: Coincident(g8,g9)
    c: Block(g7)
    c: Block(g8)
    c: Weight(g10) = 1
    c: Equal(g10,g11)
    c: Equal(g10,g12)
    c: InternalAlignment(g10,g13)
    c: InternalAlignment(g11,g13)
    c: InternalAlignment(g12,g13)
    c: InternalAlignment(g14,g13)
    c: InternalAlignment(g15,g13)
    c: Weight(g16) = 1
    c: Equal(g16,g17)
    c: Equal(g16,g18)
    c: InternalAlignment(g16,g19)
    c: InternalAlignment(g17,g19)
    c: InternalAlignment(g18,g19)
    c: InternalAlignment(g20,g19)
    c: InternalAlignment(g21,g19)
    c: Block(g19)
    c: Block(g13)
    c: Weight(g22) = 1
    c: Equal(g22,g23)
    c: Equal(g22,g24)
    c: InternalAlignment(g22,g25)
    c: InternalAlignment(g23,g25)
    c: InternalAlignment(g24,g25)
    c: InternalAlignment(g26,g25)
    c: InternalAlignment(g27,g25)
    c: Weight(g28) = 1
    c: Equal(g28,g29)
    c: Equal(g28,g30)
    c: InternalAlignment(g28,g31)
    c: InternalAlignment(g29,g31)
    c: InternalAlignment(g30,g31)
    c: InternalAlignment(g32,g31)
    c: InternalAlignment(g33,g31)
    c: Block(g31)
    c: Block(g25)
    c: Weight(g34) = 1
    c: Equal(g34,g35)
    c: Equal(g34,g36)
    c: InternalAlignment(g34,g37)
    c: InternalAlignment(g35,g37)
    c: InternalAlignment(g36,g37)
    c: InternalAlignment(g38,g37)
    c: InternalAlignment(g39,g37)
    c: Weight(g40) = 1
    c: Equal(g40,g41)
    c: Equal(g40,g42)
    c: InternalAlignment(g40,g43)
    c: InternalAlignment(g41,g43)
    c: InternalAlignment(g42,g43)
    c: InternalAlignment(g44,g43)
    c: InternalAlignment(g45,g43)
    c: Block(g37)
    c: Block(g43)
    c: Coincident(g46,g4)
    c: Coincident(g46,g3)
    c: Horizontal(g46)
    c: Distance(g46) = 450
    c: Coincident(g47,g4)
    c: Coincident(g47,g3)
    c: Horizontal(g47)
    c: Horizontal(g48)
    c: Coincident(g2,g48)
    c: Block(g48)
    c: Coincident(g1,g48)
    c: Weight(g49) = 1
    c: Equal(g49,g50)
    c: Equal(g49,g51)
    c: InternalAlignment(g49,g52)
    c: InternalAlignment(g50,g52)
    c: InternalAlignment(g51,g52)
    c: InternalAlignment(g53,g52)
    c: InternalAlignment(g54,g52)
    c: Block(g52)
    c: Weight(g55) = 1
    c: Equal(g55,g56)
    c: Equal(g55,g57)
    c: InternalAlignment(g55,g58)
    c: InternalAlignment(g56,g58)
    c: InternalAlignment(g57,g58)
    c: InternalAlignment(g59,g58)
    c: InternalAlignment(g60,g58)
    c: Block(g58)
    c: Weight(g61) = 1
    c: Equal(g61,g62)
    c: Equal(g61,g63)
    c: InternalAlignment(g61,g64)
    c: InternalAlignment(g62,g64)
    c: InternalAlignment(g63,g64)
    c: InternalAlignment(g65,g64)
    c: InternalAlignment(g66,g64)
    c: Block(g64)
    c: Weight(g67) = 1
    c: Equal(g67,g68)
    c: Equal(g67,g69)
    c: InternalAlignment(g67,g70)
    c: InternalAlignment(g68,g70)
    c: InternalAlignment(g69,g70)
    c: InternalAlignment(g71,g70)
    c: InternalAlignment(g72,g70)
    c: Block(g70)
    c: Weight(g73) = 1
    c: Equal(g73,g74)
    c: Equal(g73,g75)
    c: InternalAlignment(g73,g76)
    c: InternalAlignment(g74,g76)
    c: InternalAlignment(g75,g76)
    c: InternalAlignment(g77,g76)
    c: InternalAlignment(g78,g76)
    c: Weight(g79) = 1
    c: Equal(g79,g80)
    c: Equal(g79,g81)
    c: InternalAlignment(g79,g82)
    c: InternalAlignment(g80,g82)
    c: InternalAlignment(g81,g82)
    c: InternalAlignment(g83,g82)
    c: InternalAlignment(g84,g82)
    c: Block(g76)
    c: Block(g82)
    c: Coincident(g85,g76)
    c: Coincident(g85,g82)
    c: Vertical(g85)
    c: Coincident(g86,g76)
    c: Coincident(g86,g58)
    c: Coincident(g87,g58)
    c: Coincident(g87,g82)
    c: Weight(g88) = 1
    c: Equal(g88,g89)
    c: Equal(g88,g90)
    c: InternalAlignment(g88,g91)
    c: InternalAlignment(g89,g91)
    c: InternalAlignment(g90,g91)
    c: InternalAlignment(g92,g91)
    c: InternalAlignment(g93,g91)
    c: Weight(g94) = 1
    c: Equal(g94,g95)
    c: Equal(g94,g96)
    c: InternalAlignment(g94,g97)
    c: InternalAlignment(g95,g97)
    c: InternalAlignment(g96,g97)
    c: InternalAlignment(g98,g97)
    c: InternalAlignment(g99,g97)
    c: Block(g91)
    c: Block(g97)
    c: Coincident(g100,g91)
    c: Coincident(g100,g97)
    c: Vertical(g100)
    c: Coincident(g101,g91)
    c: Coincident(g101,g52)
    c: Coincident(g102,g52)
    c: Coincident(g102,g97)
    c: Weight(g103) = 1
    c: Equal(g103,g104)
    c: Equal(g103,g105)
    c: InternalAlignment(g103,g106)
    c: InternalAlignment(g104,g106)
    c: InternalAlignment(g105,g106)
    c: InternalAlignment(g107,g106)
    c: InternalAlignment(g108,g106)
    c: Weight(g109) = 1
    c: Equal(g109,g110)
    c: Equal(g109,g111)
    c: InternalAlignment(g109,g112)
    c: InternalAlignment(g110,g112)
    c: InternalAlignment(g111,g112)
    c: InternalAlignment(g113,g112)
    c: InternalAlignment(g114,g112)
    c: Block(g106)
    c: Block(g112)
    c: Coincident(g115,g106)
    c: Coincident(g115,g112)
    c: Vertical(g115)
    c: Coincident(g116,g112)
    c: Coincident(g116,g70)
    c: Coincident(g117,g70)
    c: Coincident(g117,g106)
    c: Weight(g118) = 1
    c: Equal(g118,g119)
    c: Equal(g118,g120)
    c: InternalAlignment(g118,g121)
    c: InternalAlignment(g119,g121)
    c: InternalAlignment(g120,g121)
    c: InternalAlignment(g122,g121)
    c: InternalAlignment(g123,g121)
    c: Weight(g124) = 1
    c: Equal(g124,g125)
    c: Equal(g124,g126)
    c: InternalAlignment(g124,g127)
    c: InternalAlignment(g125,g127)
    c: InternalAlignment(g126,g127)
    c: InternalAlignment(g128,g127)
    c: InternalAlignment(g129,g127)
    c: Block(g121)
    c: Block(g127)
    c: Coincident(g130,g121)
    c: Coincident(g130,g127)
    c: Vertical(g130)
    c: Coincident(g131,g127)
    c: Coincident(g131,g64)
    c: Coincident(g132,g64)
    c: Coincident(g132,g121)
    c: Weight(g133) = 1
    c: Equal(g133,g134)
    c: Equal(g133,g135)
    c: InternalAlignment(g133,g136)
    c: InternalAlignment(g134,g136)
    c: InternalAlignment(g135,g136)
    c: InternalAlignment(g137,g136)
    c: InternalAlignment(g138,g136)
    c: Weight(g139) = 1
    c: Equal(g139,g140)
    c: Equal(g139,g141)
    c: InternalAlignment(g139,g142)
    c: InternalAlignment(g140,g142)
    c: InternalAlignment(g141,g142)
    c: InternalAlignment(g143,g142)
    c: InternalAlignment(g144,g142)
    c: Weight(g145) = 1
    c: Equal(g145,g146)
    c: Equal(g145,g147)
    c: InternalAlignment(g145,g148)
    c: InternalAlignment(g146,g148)
    c: InternalAlignment(g147,g148)
    c: InternalAlignment(g149,g148)
    c: InternalAlignment(g150,g148)
    c: Weight(g151) = 1
    c: Equal(g151,g152)
    c: Equal(g151,g153)
    c: InternalAlignment(g151,g154)
    c: InternalAlignment(g152,g154)
    c: InternalAlignment(g153,g154)
    c: InternalAlignment(g155,g154)
    c: InternalAlignment(g156,g154)
    c: Block(g154)
    c: Block(g148)
    c: Block(g142)
    c: Block(g136)
    c: Coincident(g157,g31)
    c: Coincident(g157,g154)
    c: Coincident(g158,g154)
    c: Coincident(g158,g148)
    c: Horizontal(g158)
    c: Coincident(g159,g148)
    c: Coincident(g159,g31)
    c: Vertical(g159)
    c: Coincident(g160,g25)
    c: Coincident(g160,g142)
    c: Vertical(g160)
    c: Coincident(g161,g142)
    c: Coincident(g161,g136)
    c: Horizontal(g161)
    c: Coincident(g162,g136)
    c: Coincident(g162,g25)
    c: Weight(g163) = 1
    c: Equal(g163,g164)
    c: Equal(g163,g165)
    c: InternalAlignment(g163,g166)
    c: InternalAlignment(g164,g166)
    c: InternalAlignment(g165,g166)
    c: InternalAlignment(g167,g166)
    c: InternalAlignment(g168,g166)
    c: Weight(g169) = 1
    c: Equal(g169,g170)
    c: Equal(g169,g171)
    c: InternalAlignment(g169,g172)
    c: InternalAlignment(g170,g172)
    c: InternalAlignment(g171,g172)
    c: InternalAlignment(g173,g172)
    c: InternalAlignment(g174,g172)
    c: Weight(g175) = 1
    c: Equal(g175,g176)
    c: Equal(g175,g177)
    c: InternalAlignment(g175,g178)
    c: InternalAlignment(g176,g178)
    c: InternalAlignment(g177,g178)
    c: InternalAlignment(g179,g178)
    c: InternalAlignment(g180,g178)
    c: Weight(g181) = 1
    c: Equal(g181,g182)
    c: Equal(g181,g183)
    c: InternalAlignment(g181,g184)
    c: InternalAlignment(g182,g184)
    c: InternalAlignment(g183,g184)
    c: InternalAlignment(g185,g184)
    c: InternalAlignment(g186,g184)
    c: Block(g184)
    c: Block(g178)
    c: Block(g172)
    c: Block(g166)
    c: Coincident(g187,g184)
    c: Coincident(g187,g178)
    c: Horizontal(g187)
    c: Coincident(g188,g178)
    c: Coincident(g188,g13)
    c: Vertical(g188)
    c: Coincident(g189,g19)
    c: Coincident(g189,g172)
    c: Vertical(g189)
    c: Coincident(g190,g172)
    c: Coincident(g190,g166)
    c: Horizontal(g190)
    c: Coincident(g191,g166)
    c: Coincident(g191,g19)
    c: Coincident(g192,g13)
    c: Weight(g193) = 1
    c: Equal(g193,g194)
    c: Equal(g193,g195)
    c: InternalAlignment(g193,g196)
    c: InternalAlignment(g194,g196)
    c: InternalAlignment(g195,g196)
    c: InternalAlignment(g197,g196)
    c: InternalAlignment(g198,g196)
    c: Weight(g199) = 1
    c: Equal(g199,g200)
    c: Equal(g199,g201)
    c: InternalAlignment(g199,g202)
    c: InternalAlignment(g200,g202)
    c: InternalAlignment(g201,g202)
    c: InternalAlignment(g203,g202)
    c: InternalAlignment(g204,g202)
    c: Block(g202)
    c: Block(g196)
    c: Coincident(g205,g202)
    c: Coincident(g205,g37)
    c: Coincident(g206,g37)
    c: Coincident(g206,g196)
    c: Coincident(g207,g196)
    c: Coincident(g207,g202)
    c: Vertical(g207)
    c: Weight(g208) = 1
    c: Equal(g208,g209)
    c: Equal(g208,g210)
    c: InternalAlignment(g208,g211)
    c: InternalAlignment(g209,g211)
    c: InternalAlignment(g210,g211)
    c: InternalAlignment(g212,g211)
    c: InternalAlignment(g213,g211)
    c: Weight(g214) = 1
    c: Equal(g214,g215)
    c: Equal(g214,g216)
    c: InternalAlignment(g214,g217)
    c: InternalAlignment(g215,g217)
    c: InternalAlignment(g216,g217)
    c: InternalAlignment(g218,g217)
    c: InternalAlignment(g219,g217)
    c: Block(g217)
    c: Block(g211)
    c: Coincident(g220,g211)
    c: Coincident(g220,g43)
    c: Coincident(g221,g43)
    c: Coincident(g221,g217)
    c: Coincident(g222,g217)
    c: Coincident(g222,g211)
    c: Vertical(g222)
    c: Horizontal(g223)
    c: Block(g223)
    c: Vertical(g224)
    c: Block(g224)
    c: Block(g225)
    c: Weight(g226) = 1
    c: Equal(g226,g227)
    c: Equal(g226,g228)
    c: InternalAlignment(g226,g229)
    c: InternalAlignment(g227,g229)
    c: InternalAlignment(g228,g229)
    c: InternalAlignment(g230,g229)
    c: InternalAlignment(g231,g229)
    c: Weight(g232) = 1
    c: Equal(g232,g233)
    c: Equal(g232,g234)
    c: InternalAlignment(g232,g235)
    c: InternalAlignment(g233,g235)
    c: InternalAlignment(g234,g235)
    c: InternalAlignment(g236,g235)
    c: InternalAlignment(g237,g235)
    c: Weight(g238) = 1
    c: Equal(g238,g239)
    c: Equal(g238,g240)
    c: InternalAlignment(g238,g241)
    c: InternalAlignment(g239,g241)
    c: InternalAlignment(g240,g241)
    c: InternalAlignment(g242,g241)
    c: InternalAlignment(g243,g241)
    c: Weight(g244) = 1
    c: Equal(g244,g245)
    c: Equal(g244,g246)
    c: InternalAlignment(g244,g247)
    c: InternalAlignment(g245,g247)
    c: InternalAlignment(g246,g247)
    c: InternalAlignment(g248,g247)
    c: InternalAlignment(g249,g247)
    c: Block(g229)
    c: Block(g235)
    c: Block(g241)
    c: Block(g247)
    c: Coincident(g250,g235)
    c: Coincident(g250,g229)
    c: Horizontal(g250)
    c: Block(g192)
    c: Weight(g251) = 1
    c: Equal(g251,g252)
    c: Equal(g251,g253)
    c: InternalAlignment(g251,g254)
    c: InternalAlignment(g252,g254)
    c: InternalAlignment(g253,g254)
    c: InternalAlignment(g255,g254)
    c: InternalAlignment(g256,g254)
    c: Weight(g257) = 1
    c: Equal(g257,g258)
    c: Equal(g257,g259)
    c: InternalAlignment(g257,g260)
    c: InternalAlignment(g258,g260)
    c: InternalAlignment(g259,g260)
    c: InternalAlignment(g261,g260)
    c: InternalAlignment(g262,g260)
    c: Block(g254)
    c: Block(g260)
    c: Coincident(g263,g254)
    c: Coincident(g263,g260)
    c: Weight(g264) = 1
    c: Equal(g264,g265)
    c: Equal(g264,g266)
    c: InternalAlignment(g264,g267)
    c: InternalAlignment(g265,g267)
    c: InternalAlignment(g266,g267)
    c: InternalAlignment(g268,g267)
    c: InternalAlignment(g269,g267)
    c: Weight(g270) = 1
    c: Equal(g270,g271)
    c: Equal(g270,g272)
    c: InternalAlignment(g270,g273)
    c: InternalAlignment(g271,g273)
    c: InternalAlignment(g272,g273)
    c: InternalAlignment(g274,g273)
    c: InternalAlignment(g275,g273)
    c: Weight(g276) = 1
    c: Equal(g276,g277)
    c: Equal(g276,g278)
    c: InternalAlignment(g276,g279)
    c: InternalAlignment(g277,g279)
    c: InternalAlignment(g278,g279)
    c: InternalAlignment(g280,g279)
    c: InternalAlignment(g281,g279)
    c: Block(g279)
    c: Block(g273)
    c: Block(g267)
    c: Coincident(g282,g273)
    c: Coincident(g282,g267)
    c: Coincident(g283,g267)
    c: Coincident(g283,g279)
    c: Vertical(g283)
    c: Coincident(g284,g279)
    c: Coincident(g284,g273)
    c: Horizontal(g284)
    c: Weight(g285) = 1
    c: Equal(g285,g286)
    c: InternalAlignment(g285,g287)
    c: InternalAlignment(g286,g287)
    c: InternalAlignment(g288,g287)
    c: InternalAlignment(g289,g287)
    c: Weight(g290) = 1
    c: InternalAlignment(g291,g293)
    c: InternalAlignment(g292,g293)
    c: InternalAlignment(g294,g293)
    c: InternalAlignment(g295,g293)
    c: Weight(g296) = 1
    c: Equal(g296,g297)
    c: Equal(g296,g298)
    c: InternalAlignment(g296,g299)
    c: InternalAlignment(g297,g299)
    c: InternalAlignment(g298,g299)
    c: InternalAlignment(g300,g299)
    c: InternalAlignment(g301,g299)
    c: Equal(g302,g303)
    c: Equal(g302,g304)
    c: InternalAlignment(g302,g305)
    c: InternalAlignment(g303,g305)
    c: InternalAlignment(g304,g305)
    c: InternalAlignment(g306,g305)
    c: InternalAlignment(g307,g305)
    c: Block(g293)
    c: Block(g299)
    c: Block(g305)
    c: Block(g287)
    c: Coincident(g308,g287)
    c: Coincident(g308,g293)
    c: Horizontal(g308)
    c: Coincident(g309,g293)
    c: Coincident(g309,g299)
    c: Vertical(g309)
    c: Coincident(g310,g299)
    c: Coincident(g310,g305)
    c: Horizontal(g310)
    c: Coincident(g311,g305)
    c: Coincident(g311,g287)
    c: Weight(g312) = 1
    c: Equal(g312,g313)
    c: Equal(g312,g314)
    c: InternalAlignment(g312,g315)
    c: InternalAlignment(g313,g315)
    c: InternalAlignment(g314,g315)
    c: InternalAlignment(g316,g315)
    c: InternalAlignment(g317,g315)
    c: Weight(g318) = 1
    c: Equal(g318,g319)
    c: Equal(g318,g320)
    c: InternalAlignment(g318,g321)
    c: InternalAlignment(g319,g321)
    c: InternalAlignment(g320,g321)
    c: InternalAlignment(g322,g321)
    c: InternalAlignment(g323,g321)
    c: Weight(g324) = 1
    c: Equal(g324,g325)
    c: Equal(g324,g326)
    c: InternalAlignment(g324,g327)
    c: InternalAlignment(g325,g327)
    c: InternalAlignment(g326,g327)
    c: InternalAlignment(g328,g327)
    c: InternalAlignment(g329,g327)
    c: Block(g327)
    c: Block(g321)
    c: Block(g315)
    c: Coincident(g330,g327)
    c: Coincident(g330,g321)
    c: Horizontal(g330)
    c: Coincident(g331,g321)
    c: Coincident(g331,g315)
    c: Vertical(g331)
    c: Coincident(g332,g315)
    c: Coincident(g332,g327)
    c: InternalAlignment(g333,g334)
    c: InternalAlignment(g335,g334)
    c: InternalAlignment(g336,g334)
    c: Block(g334)
    c: Equal(g337,g338)
    c: Equal(g337,g339)
    c: InternalAlignment(g337,g340)
    c: InternalAlignment(g338,g340)
    c: InternalAlignment(g339,g340)
    c: InternalAlignment(g341,g340)
    c: InternalAlignment(g342,g340)
    c: Block(g340)
    c: Coincident(g343,g334)
    c: Horizontal(g343)
    c: Block(g343)
    c: Coincident(g344,g334)
    c: Coincident(g344,g260)
    c: Vertical(g344)
    c: Coincident(g345,g340)
    c: Coincident(g345,g254)
    c: Vertical(g345)
    c: Coincident(g347,g5)
    c: Coincident(g348,g5)
    c: Block(g346)
    c: Block(g5)
    c: Block(g348)
    c: Block(g347)
    c: Distance(g344) = 119.89
FEATURE [Sketcher::SketchObject] Sketch001
  FullyConstrained = true
  MapMode = 4
  Placement = pos=(0,0,0) rot=(0.57735,0.57735,0.57735;2.0944rad)
  Support = -> [Sketch]
  sketch-geometry (46):
    g0: BSplineCurve PolesCount=3 KnotsCount=2 Degree=2 IsPeriodic=0
    g1: ArcOfCircle CenterX=73.1223 CenterY=-32.291 CenterZ=0 NormalX=0 NormalY=0 NormalZ=1 AngleXU=0 Radius=13 StartAngle=5.92268 EndAngle=9.06428
    g2: ArcOfCircle CenterX=66.7816 CenterY=-49.1439 CenterZ=0 NormalX=0 NormalY=0 NormalZ=1 AngleXU=0 Radius=13 StartAngle=2.78068 EndAngle=5.92131
    g3: ArcOfCircle CenterX=55.9263 CenterY=-78.1807 CenterZ=0 NormalX=0 NormalY=0 NormalZ=1 AngleXU=0 Radius=13 StartAngle=5.92268 EndAngle=9.06428
    g4: ArcOfCircle CenterX=49.5884 CenterY=-95.0342 CenterZ=0 NormalX=0 NormalY=0 NormalZ=1 AngleXU=0 Radius=13 StartAngle=2.78068 EndAngle=5.92131
    g5: ArcOfCircle CenterX=38.7206 CenterY=-124.067 CenterZ=0 NormalX=0 NormalY=0 NormalZ=1 AngleXU=0 Radius=13 StartAngle=5.92268 EndAngle=9.06428
    g6: ArcOfCircle CenterX=32.3875 CenterY=-140.92 CenterZ=0 NormalX=0 NormalY=0 NormalZ=1 AngleXU=0 Radius=13 StartAngle=2.78068 EndAngle=5.92131
    g7: ArcOfCircle CenterX=21.4715 CenterY=-169.934 CenterZ=0 NormalX=0 NormalY=0 NormalZ=1 AngleXU=0 Radius=13 StartAngle=5.92268 EndAngle=9.06428
    g8: ArcOfCircle CenterX=15.1336 CenterY=-186.787 CenterZ=0 NormalX=0 NormalY=0 NormalZ=1 AngleXU=0 Radius=13 StartAngle=2.78068 EndAngle=5.92131
    g9-g12: Circle x4 (B-spline internal-alignment scaffolding for g13; pole/knot coordinates omitted)
    g13: BSplineCurve PolesCount=4 KnotsCount=2 Degree=3 IsPeriodic=0
    g14: GeomPoint X=28.8094 Y=-19.0875 Z=0
    g15: GeomPoint X=47.0443 Y=-50.4712 Z=0
    g16: Circle CenterX=53.5586 CenterY=-23.2695 CenterZ=0 NormalX=0 NormalY=0 NormalZ=1 AngleXU=0 Radius=3.24518
    g17: Circle CenterX=-195.441 CenterY=-127.082 CenterZ=0 NormalX=0 NormalY=0 NormalZ=1 AngleXU=0 Radius=1
    g18: Circle CenterX=-8.24091 CenterY=-197.481 CenterZ=0 NormalX=0 NormalY=0 NormalZ=1 AngleXU=0 Radius=1
    g19: Circle CenterX=12.8789 CenterY=-141.321 CenterZ=0 NormalX=0 NormalY=0 NormalZ=1 AngleXU=0 Radius=1
    g20: BSplineCurve PolesCount=3 KnotsCount=2 Degree=2 IsPeriodic=0
    g21: GeomPoint X=-195.441 Y=-127.082 Z=0
    g22: GeomPoint X=12.8789 Y=-141.321 Z=0
    g23: Circle CenterX=-12.8016 CenterY=-179.036 CenterZ=0 NormalX=0 NormalY=0 NormalZ=1 AngleXU=0 Radius=10.5072
    g24: Circle CenterX=0.933922 CenterY=-166.43 CenterZ=0 NormalX=0 NormalY=0 NormalZ=1 AngleXU=0 Radius=3.26661
    g25: Circle CenterX=-33.5518 CenterY=-176.44 CenterZ=0 NormalX=0 NormalY=0 NormalZ=1 AngleXU=0 Radius=5.64388
    g26: Circle CenterX=-47.2366 CenterY=-173.859 CenterZ=0 NormalX=0 NormalY=0 NormalZ=1 AngleXU=0 Radius=3.01653
    g27: Circle CenterX=-56.2595 CenterY=-171.456 CenterZ=0 NormalX=0 NormalY=0 NormalZ=1 AngleXU=0 Radius=2.12826
    g28: ArcOfCircle CenterX=51.2151 CenterY=-198.473 CenterZ=0 NormalX=0 NormalY=0 NormalZ=1 AngleXU=0 Radius=20 StartAngle=2.78189 EndAngle=4.35269
    g29: LineSegment StartX=32.4951 StartY=-191.433 StartZ=0 EndX=94.6578 EndY=-26.1352 EndZ=0
    g30: LineSegment StartX=43.1192 StartY=-220.001 StartZ=0 EndX=-196.497 EndY=-129.89 EndZ=0
    g31: LineSegment StartX=43.1192 StartY=-220.001 StartZ=0 EndX=44.1752 EndY=-217.193 EndZ=0
    g32: LineSegment StartX=117.223 StartY=-19.0875 StartZ=0 EndX=117.223 EndY=-16.0875 EndZ=0
    g33: LineSegment StartX=117.223 StartY=-16.0875 StartZ=0 EndX=17.2232 EndY=-16.0875 EndZ=0
    g34: LineSegment StartX=17.2232 StartY=-16.0875 StartZ=0 EndX=17.2232 EndY=-19.0875 EndZ=0
    g35: LineSegment StartX=28.8094 StartY=-19.0875 StartZ=0 EndX=17.2232 EndY=-19.0875 EndZ=0
    g36: LineSegment StartX=47.0443 StartY=-50.4712 StartZ=0 EndX=12.8789 EndY=-141.321 EndZ=0
    g37: LineSegment StartX=-195.441 StartY=-127.082 StartZ=0 EndX=-196.497 EndY=-129.89 EndZ=0
    g38: LineSegment StartX=85.2866 StartY=-36.8766 StartZ=0 EndX=78.9396 EndY=-53.7463 EndZ=0
    g39: LineSegment StartX=60.9579 StartY=-27.7053 StartZ=0 EndX=54.6191 EndY=-44.5532 EndZ=0
    g40: LineSegment StartX=68.0907 StartY=-82.7664 StartZ=0 EndX=61.7465 EndY=-99.6365 EndZ=0
    g41: LineSegment StartX=43.7619 StartY=-73.595 StartZ=0 EndX=37.426 EndY=-90.4435 EndZ=0
    g42: LineSegment StartX=50.885 StartY=-128.652 StartZ=0 EndX=44.5456 EndY=-145.522 EndZ=0
    g43: LineSegment StartX=26.5562 StartY=-119.481 StartZ=0 EndX=20.2251 EndY=-136.329 EndZ=0
    g44: LineSegment StartX=9.3071 StartY=-165.349 StartZ=0 EndX=2.97115 EndY=-182.197 EndZ=0
    g45: LineSegment StartX=33.6358 StartY=-174.52 StartZ=0 EndX=27.2917 EndY=-191.39 EndZ=0
  constraints (71):
    c: Block(g0)
    c: Block(g1)
    c: Block(g2)
    c: Block(g4)
    c: Block(g3)
    c: Block(g6)
    c: Block(g5)
    c: Block(g8)
    c: Block(g7)
    c: Weight(g9) = 1
    c: Equal(g9,g10)
    c: Equal(g9,g11)
    c: Equal(g9,g12)
    c: InternalAlignment(g9-g12 -> g13) x4
    c: InternalAlignment(g14,g13)
    c: InternalAlignment(g15,g13)
    c: Block(g16)
    c: Weight(g17) = 1
    c: Equal(g17,g18)
    c: Equal(g17,g19)
    c: InternalAlignment(g17,g20)
    c: InternalAlignment(g18,g20)
    c: InternalAlignment(g19,g20)
    c: InternalAlignment(g21,g20)
    c: InternalAlignment(g22,g20)
    c: Block(g20)
    c: Block(g23)
    c: Block(g24)
    c: Block(g25)
    c: Block(g26)
    c: Block(g27)
    c: Block(g28)
    c: Coincident(g29,g28)
    c: Coincident(g29,g0)
    c: Block(g13)
    c: Coincident(g31,g30)
    c: Coincident(g31,g28)
    c: Block(g31)
    c: Coincident(g32,g0)
    c: Vertical(g32)
    c: Coincident(g33,g32)
    c: Horizontal(g33)
    c: Coincident(g34,g33)
    c: Vertical(g34)
    c: Block(g33)
    c: Coincident(g35,g13)
    c: Coincident(g35,g34)
    c: Horizontal(g35)
    c: Coincident(g36,g13)
    c: Coincident(g36,g20)
    c: Coincident(g37,g20)
    c: Coincident(g37,g30)
    c: Block(g30)
    c: Coincident(g38,g1)
    c: Coincident(g38,g2)
    c: Coincident(g39,g1)
    c: Coincident(g39,g2)
    c: Coincident(g40,g3)
    c: Coincident(g40,g4)
    c: Coincident(g41,g3)
    c: Coincident(g41,g4)
    c: Coincident(g42,g5)
    c: Coincident(g42,g6)
    c: Coincident(g43,g5)
    c: Coincident(g43,g6)
    c: Coincident(g44,g7)
    c: Coincident(g44,g8)
    c: Coincident(g45,g7)
    c: Coincident(g45,g8)
    c: Distance(g30) = 256
    c: Distance(g33) = 100
FEATURE [Part::Extrusion] Extrude002
  Base = -> Sketch001
  Dir = (1,0,0)
  DirMode = 2
  FaceMakerClass = Part::FaceMakerBullseye
  LengthFwd = 8
  LengthRev = 0
  Solid = true
  Symmetric = false
FEATURE [Sketcher::SketchObject] Sketch002
  FullyConstrained = true
  sketch-geometry (20):
    g0: LineSegment StartX=-2.77179 StartY=-200.304 StartZ=0 EndX=5.22821 EndY=-200.304 EndZ=0
    g1: LineSegment StartX=5.22821 StartY=-200.304 StartZ=0 EndX=5.22821 EndY=-197.304 EndZ=0
    g2: LineSegment StartX=-2.77179 StartY=-200.304 StartZ=0 EndX=-2.77179 EndY=-197.304 EndZ=0
    g3: LineSegment StartX=5.22821 StartY=-197.304 StartZ=0 EndX=8.22821 EndY=-197.304 EndZ=0
    g4: LineSegment StartX=-2.77179 StartY=-197.304 StartZ=0 EndX=-5.77179 EndY=-197.304 EndZ=0
    g5: LineSegment StartX=19.2282 StartY=-203.304 StartZ=0 EndX=19.2282 EndY=-206.304 EndZ=0
    g6: LineSegment StartX=-16.7718 StartY=-203.304 StartZ=0 EndX=-16.7718 EndY=-206.304 EndZ=0
    g7: LineSegment StartX=-16.7718 StartY=-206.304 StartZ=0 EndX=19.2282 EndY=-206.304 EndZ=0
    g8: Circle CenterX=-16.7718 CenterY=-203.304 CenterZ=0 NormalX=0 NormalY=0 NormalZ=1 AngleXU=0 Radius=1
    g9: Circle CenterX=-5.77179 CenterY=-203.304 CenterZ=0 NormalX=0 NormalY=0 NormalZ=1 AngleXU=0 Radius=1
    g10: Circle CenterX=-5.77179 CenterY=-197.304 CenterZ=0 NormalX=0 NormalY=0 NormalZ=1 AngleXU=0 Radius=1
    g11: BSplineCurve PolesCount=3 KnotsCount=2 Degree=2 IsPeriodic=0
    g12: GeomPoint X=-16.7718 Y=-203.304 Z=0
    g13: GeomPoint X=-5.77179 Y=-197.304 Z=0
    g14: Circle CenterX=19.2282 CenterY=-203.304 CenterZ=0 NormalX=0 NormalY=0 NormalZ=1 AngleXU=0 Radius=1
    g15: Circle CenterX=8.22821 CenterY=-203.304 CenterZ=0 NormalX=0 NormalY=0 NormalZ=1 AngleXU=0 Radius=1
    g16: Circle CenterX=8.22821 CenterY=-197.304 CenterZ=0 NormalX=0 NormalY=0 NormalZ=1 AngleXU=0 Radius=1
    g17: BSplineCurve PolesCount=3 KnotsCount=2 Degree=2 IsPeriodic=0
    g18: GeomPoint X=19.2282 Y=-203.304 Z=0
    g19: GeomPoint X=8.22821 Y=-197.304 Z=0
  constraints (41):
    c: Horizontal(g0)
    c: Distance(g0) = 8
    c: Coincident(g1,g0)
    c: Vertical(g1)
    c: Distance(g1) = 3
    c: Coincident(g2,g0)
    c: Vertical(g2)
    c: Distance(g2) = 3
    c: Coincident(g3,g1)
    c: Horizontal(g3)
    c: Distance(g3) = 3
    c: Coincident(g4,g2)
    c: Horizontal(g4)
    c: Distance(g4) = 3
    c: Vertical(g5)
    c: Vertical(g6)
    c: Coincident(g7,g6)
    c: Coincident(g7,g5)
    c: Weight(g8) = 1
    c: Equal(g8,g9)
    c: Equal(g8,g10)
    c: Coincident(g11,g4)
    c: InternalAlignment(g8,g11)
    c: InternalAlignment(g9,g11)
    c: InternalAlignment(g10,g11)
    c: InternalAlignment(g12,g11)
    c: InternalAlignment(g13,g11)
    c: Coincident(g17,g5)
    c: Weight(g14) = 1
    c: Equal(g14,g15)
    c: Equal(g14,g16)
    c: Coincident(g17,g3)
    c: InternalAlignment(g14,g17)
    c: InternalAlignment(g15,g17)
    c: InternalAlignment(g16,g17)
    c: InternalAlignment(g18,g17)
    c: InternalAlignment(g19,g17)
    c: Block(g7)
    c: Block(g17)
    c: Block(g11)
    c: Block(g6)
FEATURE [Part::Extrusion] Extrude003
  Base = -> Sketch002
  Dir = (0,0,1)
  DirMode = 2
  FaceMakerClass = Part::FaceMakerBullseye
  LengthFwd = 260
  LengthRev = 0
  Solid = true
  Symmetric = false
FEATURE [Sketcher::SketchObject] Sketch003
  FullyConstrained = false
  sketch-geometry (377):
    g0: LineSegment StartX=-42.9272 StartY=136.221 StartZ=0 EndX=-42.9272 EndY=-103.779 EndZ=0
    g1: LineSegment StartX=407.073 StartY=136.221 StartZ=0 EndX=407.073 EndY=-103.779 EndZ=0
    g2: ArcOfCircle CenterX=-26.9272 CenterY=-83.7794 CenterZ=0 NormalX=0 NormalY=0 NormalZ=1 AngleXU=0 Radius=8 StartAngle=3.14159 EndAngle=6.28319
    g3: ArcOfCircle CenterX=391.073 CenterY=-83.7794 CenterZ=0 NormalX=0 NormalY=0 NormalZ=1 AngleXU=0 Radius=8 StartAngle=3.14159 EndAngle=6.28319
    g4: Circle CenterX=175.022 CenterY=27.0628 CenterZ=0 NormalX=0 NormalY=0 NormalZ=1 AngleXU=0 Radius=1
    g5: Circle CenterX=179.022 CenterY=24.8665 CenterZ=0 NormalX=0 NormalY=0 NormalZ=1 AngleXU=0 Radius=1
    g6: Circle CenterX=179.022 CenterY=27.0628 CenterZ=0 NormalX=0 NormalY=0 NormalZ=1 AngleXU=0 Radius=1
    g7: BSplineCurve PolesCount=3 KnotsCount=2 Degree=2 IsPeriodic=0
    g8: GeomPoint X=175.022 Y=27.0628 Z=0
    g9: GeomPoint X=179.022 Y=27.0628 Z=0
    g10: Circle CenterX=189.124 CenterY=27.0628 CenterZ=0 NormalX=0 NormalY=0 NormalZ=1 AngleXU=0 Radius=1
    g11: Circle CenterX=185.124 CenterY=24.8665 CenterZ=0 NormalX=0 NormalY=0 NormalZ=1 AngleXU=0 Radius=1
    g12: Circle CenterX=185.124 CenterY=27.0628 CenterZ=0 NormalX=0 NormalY=0 NormalZ=1 AngleXU=0 Radius=1
    g13: BSplineCurve PolesCount=3 KnotsCount=2 Degree=2 IsPeriodic=0
    g14: GeomPoint X=189.124 Y=27.0628 Z=0
    g15: GeomPoint X=185.124 Y=27.0628 Z=0
    g16: Circle CenterX=175.022 CenterY=5.37834 CenterZ=0 NormalX=0 NormalY=0 NormalZ=1 AngleXU=0 Radius=1
    g17: Circle CenterX=179.022 CenterY=7.57463 CenterZ=0 NormalX=0 NormalY=0 NormalZ=1 AngleXU=0 Radius=1
    g18: Circle CenterX=179.022 CenterY=5.34704 CenterZ=0 NormalX=0 NormalY=0 NormalZ=1 AngleXU=0 Radius=1
    g19: BSplineCurve PolesCount=3 KnotsCount=2 Degree=2 IsPeriodic=0
    g20: GeomPoint X=175.022 Y=5.37834 Z=0
    g21: GeomPoint X=179.022 Y=5.34704 Z=0
    g22: Circle CenterX=189.124 CenterY=5.37834 CenterZ=0 NormalX=0 NormalY=0 NormalZ=1 AngleXU=0 Radius=1
    g23: Circle CenterX=185.124 CenterY=7.57463 CenterZ=0 NormalX=0 NormalY=0 NormalZ=1 AngleXU=0 Radius=1
    g24: Circle CenterX=185.124 CenterY=5.34704 CenterZ=0 NormalX=0 NormalY=0 NormalZ=1 AngleXU=0 Radius=1
    g25: BSplineCurve PolesCount=3 KnotsCount=2 Degree=2 IsPeriodic=0
    g26: GeomPoint X=189.124 Y=5.37834 Z=0
    g27: GeomPoint X=185.124 Y=5.34704 Z=0
    g28: Circle CenterX=165.871 CenterY=18.1458 CenterZ=0 NormalX=0 NormalY=0 NormalZ=1 AngleXU=0 Radius=1
    g29: Circle CenterX=169.377 CenterY=16.2206 CenterZ=0 NormalX=0 NormalY=0 NormalZ=1 AngleXU=0 Radius=1
    g30: Circle CenterX=165.871 CenterY=14.2954 CenterZ=0 NormalX=0 NormalY=0 NormalZ=1 AngleXU=0 Radius=1
    g31: BSplineCurve PolesCount=3 KnotsCount=2 Degree=2 IsPeriodic=0
    g32: GeomPoint X=165.871 Y=18.1458 Z=0
    g33: GeomPoint X=165.871 Y=14.2954 Z=0
    g34: Circle CenterX=198.275 CenterY=18.1458 CenterZ=0 NormalX=0 NormalY=0 NormalZ=1 AngleXU=0 Radius=1
    g35: Circle CenterX=194.768 CenterY=16.2206 CenterZ=0 NormalX=0 NormalY=0 NormalZ=1 AngleXU=0 Radius=1
    g36: Circle CenterX=198.275 CenterY=14.2954 CenterZ=0 NormalX=0 NormalY=0 NormalZ=1 AngleXU=0 Radius=1
    g37: BSplineCurve PolesCount=3 KnotsCount=2 Degree=2 IsPeriodic=0
    g38: GeomPoint X=198.275 Y=18.1458 Z=0
    g39: GeomPoint X=198.275 Y=14.2954 Z=0
    g40: LineSegment StartX=407.073 StartY=-103.779 StartZ=0 EndX=-42.9272 EndY=-103.779 EndZ=0
    g41: Circle CenterX=125.607 CenterY=54.1951 CenterZ=0 NormalX=0 NormalY=0 NormalZ=1 AngleXU=0 Radius=1
    g42: Circle CenterX=139.632 CenterY=46.4944 CenterZ=0 NormalX=0 NormalY=0 NormalZ=1 AngleXU=0 Radius=1
    g43: Circle CenterX=127.326 CenterY=56.7187 CenterZ=0 NormalX=0 NormalY=0 NormalZ=1 AngleXU=0 Radius=1
    g44: BSplineCurve PolesCount=3 KnotsCount=2 Degree=2 IsPeriodic=0
    g45: GeomPoint X=125.607 Y=54.1951 Z=0
    g46: GeomPoint X=127.326 Y=56.7187 Z=0
    g47: Circle CenterX=236.821 CenterY=56.7187 CenterZ=0 NormalX=0 NormalY=0 NormalZ=1 AngleXU=0 Radius=1
    g48: Circle CenterX=224.513 CenterY=46.4944 CenterZ=0 NormalX=0 NormalY=0 NormalZ=1 AngleXU=0 Radius=1
    g49: Circle CenterX=238.538 CenterY=54.1951 CenterZ=0 NormalX=0 NormalY=0 NormalZ=1 AngleXU=0 Radius=1
    g50: BSplineCurve PolesCount=3 KnotsCount=2 Degree=2 IsPeriodic=0
    g51: GeomPoint X=236.821 Y=56.7187 Z=0
    g52: GeomPoint X=238.538 Y=54.1951 Z=0
    g53: Circle CenterX=238.538 CenterY=-21.7539 CenterZ=0 NormalX=0 NormalY=0 NormalZ=1 AngleXU=0 Radius=1
    g54: Circle CenterX=224.513 CenterY=-14.0532 CenterZ=0 NormalX=0 NormalY=0 NormalZ=1 AngleXU=0 Radius=1
    g55: Circle CenterX=236.821 CenterY=-24.2775 CenterZ=0 NormalX=0 NormalY=0 NormalZ=1 AngleXU=0 Radius=1
    g56: BSplineCurve PolesCount=3 KnotsCount=2 Degree=2 IsPeriodic=0
    g57: GeomPoint X=238.538 Y=-21.7539 Z=0
    g58: GeomPoint X=236.821 Y=-24.2775 Z=0
    g59: Circle CenterX=125.607 CenterY=-21.7539 CenterZ=0 NormalX=0 NormalY=0 NormalZ=1 AngleXU=0 Radius=1
    g60: Circle CenterX=139.632 CenterY=-14.0532 CenterZ=0 NormalX=0 NormalY=0 NormalZ=1 AngleXU=0 Radius=1
    g61: Circle CenterX=127.325 CenterY=-24.2775 CenterZ=0 NormalX=0 NormalY=0 NormalZ=1 AngleXU=0 Radius=1
    g62: BSplineCurve PolesCount=3 KnotsCount=2 Degree=2 IsPeriodic=0
    g63: GeomPoint X=125.607 Y=-21.7539 Z=0
    g64: GeomPoint X=127.325 Y=-24.2775 Z=0
    g65: Circle CenterX=302.996 CenterY=111.695 CenterZ=0 NormalX=0 NormalY=0 NormalZ=1 AngleXU=0 Radius=1
    g66: Circle CenterX=306.073 CenterY=114.251 CenterZ=0 NormalX=0 NormalY=0 NormalZ=1 AngleXU=0 Radius=1
    g67: Circle CenterX=306.073 CenterY=110.251 CenterZ=0 NormalX=0 NormalY=0 NormalZ=1 AngleXU=0 Radius=1
    g68: BSplineCurve PolesCount=3 KnotsCount=2 Degree=2 IsPeriodic=0
    g69: GeomPoint X=302.996 Y=111.695 Z=0
    g70: GeomPoint X=306.073 Y=110.251 Z=0
    g71: Circle CenterX=306.073 CenterY=95.2763 CenterZ=0 NormalX=0 NormalY=0 NormalZ=1 AngleXU=0 Radius=1
    g72: Circle CenterX=306.073 CenterY=91.2763 CenterZ=0 NormalX=0 NormalY=0 NormalZ=1 AngleXU=0 Radius=1
    g73: Circle CenterX=302.567 CenterY=89.3511 CenterZ=0 NormalX=0 NormalY=0 NormalZ=1 AngleXU=0 Radius=1
    g74: BSplineCurve PolesCount=3 KnotsCount=2 Degree=2 IsPeriodic=0
    g75: GeomPoint X=306.073 Y=95.2763 Z=0
    g76: GeomPoint X=302.567 Y=89.3511 Z=0
    g77: LineSegment StartX=306.073 StartY=110.251 StartZ=0 EndX=306.073 EndY=95.2763 EndZ=0
    g78: LineSegment StartX=302.996 StartY=111.695 StartZ=0 EndX=236.821 EndY=56.7187 EndZ=0
    g79: LineSegment StartX=238.538 StartY=54.1951 StartZ=0 EndX=302.567 EndY=89.3511 EndZ=0
    g80: Circle CenterX=61.1496 CenterY=111.695 CenterZ=0 NormalX=0 NormalY=0 NormalZ=1 AngleXU=0 Radius=1
    g81: Circle CenterX=58.0728 CenterY=114.251 CenterZ=0 NormalX=0 NormalY=0 NormalZ=1 AngleXU=0 Radius=1
    g82: Circle CenterX=58.0728 CenterY=110.251 CenterZ=0 NormalX=0 NormalY=0 NormalZ=1 AngleXU=0 Radius=1
    g83: BSplineCurve PolesCount=3 KnotsCount=2 Degree=2 IsPeriodic=0
    g84: GeomPoint X=61.1496 Y=111.695 Z=0
    g85: GeomPoint X=58.0728 Y=110.251 Z=0
    g86: Circle CenterX=61.5791 CenterY=89.3511 CenterZ=0 NormalX=0 NormalY=0 NormalZ=1 AngleXU=0 Radius=1
    g87: Circle CenterX=58.0728 CenterY=91.2763 CenterZ=0 NormalX=0 NormalY=0 NormalZ=1 AngleXU=0 Radius=1
    g88: Circle CenterX=58.0728 CenterY=95.2763 CenterZ=0 NormalX=0 NormalY=0 NormalZ=1 AngleXU=0 Radius=1
    g89: BSplineCurve PolesCount=3 KnotsCount=2 Degree=2 IsPeriodic=0
    g90: GeomPoint X=61.5791 Y=89.3511 Z=0
    g91: GeomPoint X=58.0728 Y=95.2763 Z=0
    g92: LineSegment StartX=58.0728 StartY=110.251 StartZ=0 EndX=58.0728 EndY=95.2763 EndZ=0
    g93: LineSegment StartX=61.1496 StartY=111.695 StartZ=0 EndX=127.326 EndY=56.7187 EndZ=0
    g94: LineSegment StartX=125.607 StartY=54.1951 StartZ=0 EndX=61.5791 EndY=89.3511 EndZ=0
    g95: Circle CenterX=61.5791 CenterY=-56.9099 CenterZ=0 NormalX=0 NormalY=0 NormalZ=1 AngleXU=0 Radius=1
    g96: Circle CenterX=58.0728 CenterY=-58.8351 CenterZ=0 NormalX=0 NormalY=0 NormalZ=1 AngleXU=0 Radius=1
    g97: Circle CenterX=58.0728 CenterY=-62.8351 CenterZ=0 NormalX=0 NormalY=0 NormalZ=1 AngleXU=0 Radius=1
    g98: BSplineCurve PolesCount=3 KnotsCount=2 Degree=2 IsPeriodic=0
    g99: GeomPoint X=61.5791 Y=-56.9099 Z=0
    g100: GeomPoint X=58.0728 Y=-62.8351 Z=0
    g101: Circle CenterX=58.0728 CenterY=-77.8102 CenterZ=0 NormalX=0 NormalY=0 NormalZ=1 AngleXU=0 Radius=1
    g102: Circle CenterX=58.0728 CenterY=-81.8102 CenterZ=0 NormalX=0 NormalY=0 NormalZ=1 AngleXU=0 Radius=1
    g103: Circle CenterX=61.1496 CenterY=-79.2541 CenterZ=0 NormalX=0 NormalY=0 NormalZ=1 AngleXU=0 Radius=1
    g104: BSplineCurve PolesCount=3 KnotsCount=2 Degree=2 IsPeriodic=0
    g105: GeomPoint X=58.0728 Y=-77.8102 Z=0
    g106: GeomPoint X=61.1496 Y=-79.2541 Z=0
    g107: LineSegment StartX=58.0728 StartY=-62.8351 StartZ=0 EndX=58.0728 EndY=-77.8102 EndZ=0
    g108: LineSegment StartX=61.1496 StartY=-79.2541 StartZ=0 EndX=127.325 EndY=-24.2775 EndZ=0
    g109: LineSegment StartX=125.607 StartY=-21.7539 StartZ=0 EndX=61.5791 EndY=-56.9099 EndZ=0
    g110: Circle CenterX=302.567 CenterY=-56.9099 CenterZ=0 NormalX=0 NormalY=0 NormalZ=1 AngleXU=0 Radius=1
    g111: Circle CenterX=306.073 CenterY=-58.8351 CenterZ=0 NormalX=0 NormalY=0 NormalZ=1 AngleXU=0 Radius=1
    g112: Circle CenterX=306.073 CenterY=-62.8351 CenterZ=0 NormalX=0 NormalY=0 NormalZ=1 AngleXU=0 Radius=1
    g113: BSplineCurve PolesCount=3 KnotsCount=2 Degree=2 IsPeriodic=0
    g114: GeomPoint X=302.567 Y=-56.9099 Z=0
    g115: GeomPoint X=306.073 Y=-62.8351 Z=0
    g116: Circle CenterX=302.996 CenterY=-79.2541 CenterZ=0 NormalX=0 NormalY=0 NormalZ=1 AngleXU=0 Radius=1
    g117: Circle CenterX=306.073 CenterY=-81.8102 CenterZ=0 NormalX=0 NormalY=0 NormalZ=1 AngleXU=0 Radius=1
    g118: Circle CenterX=306.073 CenterY=-77.8102 CenterZ=0 NormalX=0 NormalY=0 NormalZ=1 AngleXU=0 Radius=1
    g119: BSplineCurve PolesCount=3 KnotsCount=2 Degree=2 IsPeriodic=0
    g120: GeomPoint X=302.996 Y=-79.2541 Z=0
    g121: GeomPoint X=306.073 Y=-77.8102 Z=0
    g122: LineSegment StartX=306.073 StartY=-62.8351 StartZ=0 EndX=306.073 EndY=-77.8102 EndZ=0
    g123: LineSegment StartX=302.996 StartY=-79.2541 StartZ=0 EndX=236.821 EndY=-24.2775 EndZ=0
    g124: LineSegment StartX=238.538 StartY=-21.7539 StartZ=0 EndX=302.567 EndY=-56.9099 EndZ=0
    g125: Circle CenterX=61.6457 CenterY=-88.8112 CenterZ=0 NormalX=0 NormalY=0 NormalZ=1 AngleXU=0 Radius=1
    g126: Circle CenterX=58.0728 CenterY=-91.7794 CenterZ=0 NormalX=0 NormalY=0 NormalZ=1 AngleXU=0 Radius=1
    g127: Circle CenterX=63.9135 CenterY=-91.7794 CenterZ=0 NormalX=0 NormalY=0 NormalZ=1 AngleXU=0 Radius=1
    g128: BSplineCurve PolesCount=3 KnotsCount=2 Degree=2 IsPeriodic=0
    g129: GeomPoint X=61.6457 Y=-88.8112 Z=0
    g130: GeomPoint X=63.9135 Y=-91.7794 Z=0
    g131: Circle CenterX=179.022 CenterY=-85.8163 CenterZ=0 NormalX=0 NormalY=0 NormalZ=1 AngleXU=0 Radius=1
    g132: Circle CenterX=179.022 CenterY=-91.7794 CenterZ=0 NormalX=0 NormalY=0 NormalZ=1 AngleXU=0 Radius=1
    g133: Circle CenterX=171.895 CenterY=-91.7794 CenterZ=0 NormalX=0 NormalY=0 NormalZ=1 AngleXU=0 Radius=1
    g134: BSplineCurve PolesCount=3 KnotsCount=2 Degree=2 IsPeriodic=0
    g135: GeomPoint X=179.022 Y=-85.8163 Z=0
    g136: GeomPoint X=171.895 Y=-91.7794 Z=0
    g137: Circle CenterX=185.124 CenterY=-86.2028 CenterZ=0 NormalX=0 NormalY=0 NormalZ=1 AngleXU=0 Radius=1
    g138: Circle CenterX=185.124 CenterY=-91.7794 CenterZ=0 NormalX=0 NormalY=0 NormalZ=1 AngleXU=0 Radius=1
    g139: Circle CenterX=191.747 CenterY=-91.7794 CenterZ=0 NormalX=0 NormalY=0 NormalZ=1 AngleXU=0 Radius=1
    g140: BSplineCurve PolesCount=3 KnotsCount=2 Degree=2 IsPeriodic=0
    g141: GeomPoint X=185.124 Y=-86.2028 Z=0
    g142: GeomPoint X=191.747 Y=-91.7794 Z=0
    g143: Circle CenterX=299.888 CenterY=-86.6413 CenterZ=0 NormalX=0 NormalY=0 NormalZ=1 AngleXU=0 Radius=1
    g144: Circle CenterX=306.073 CenterY=-91.7794 CenterZ=0 NormalX=0 NormalY=0 NormalZ=1 AngleXU=0 Radius=1
    g145: Circle CenterX=298.776 CenterY=-91.7794 CenterZ=0 NormalX=0 NormalY=0 NormalZ=1 AngleXU=0 Radius=1
    g146: BSplineCurve PolesCount=3 KnotsCount=2 Degree=2 IsPeriodic=0
    g147: GeomPoint X=299.888 Y=-86.6413 Z=0
    g148: GeomPoint X=298.776 Y=-91.7794 Z=0
    g149: LineSegment StartX=189.124 StartY=5.37834 StartZ=0 EndX=299.888 EndY=-86.6413 EndZ=0
    g150: LineSegment StartX=298.776 StartY=-91.7794 StartZ=0 EndX=191.747 EndY=-91.7794 EndZ=0
    g151: LineSegment StartX=185.124 StartY=-86.2028 StartZ=0 EndX=185.124 EndY=5.34704 EndZ=0
    g152: LineSegment StartX=179.022 StartY=5.34704 StartZ=0 EndX=179.022 EndY=-85.8163 EndZ=0
    g153: LineSegment StartX=171.895 StartY=-91.7794 StartZ=0 EndX=63.9135 EndY=-91.7794 EndZ=0
    g154: LineSegment StartX=61.6457 StartY=-88.8112 StartZ=0 EndX=175.022 EndY=5.37834 EndZ=0
    g155: Circle CenterX=302.073 CenterY=124.221 CenterZ=0 NormalX=0 NormalY=0 NormalZ=1 AngleXU=0 Radius=1
    g156: Circle CenterX=306.073 CenterY=124.221 CenterZ=0 NormalX=0 NormalY=0 NormalZ=1 AngleXU=0 Radius=1
    g157: Circle CenterX=302.996 CenterY=121.665 CenterZ=0 NormalX=0 NormalY=0 NormalZ=1 AngleXU=0 Radius=1
    g158: BSplineCurve PolesCount=3 KnotsCount=2 Degree=2 IsPeriodic=0
    g159: GeomPoint X=302.073 Y=124.221 Z=0
    g160: GeomPoint X=302.996 Y=121.665 Z=0
    g161: Circle CenterX=189.124 CenterY=124.221 CenterZ=0 NormalX=0 NormalY=0 NormalZ=1 AngleXU=0 Radius=1
    g162: Circle CenterX=185.124 CenterY=124.221 CenterZ=0 NormalX=0 NormalY=0 NormalZ=1 AngleXU=0 Radius=1
    g163: Circle CenterX=185.124 CenterY=120.221 CenterZ=0 NormalX=0 NormalY=0 NormalZ=1 AngleXU=0 Radius=1
    g164: BSplineCurve PolesCount=3 KnotsCount=2 Degree=2 IsPeriodic=0
    g165: GeomPoint X=189.124 Y=124.221 Z=0
    g166: GeomPoint X=185.124 Y=120.221 Z=0
    g167: Circle CenterX=175.022 CenterY=124.221 CenterZ=0 NormalX=0 NormalY=0 NormalZ=1 AngleXU=0 Radius=1
    g168: Circle CenterX=179.022 CenterY=124.221 CenterZ=0 NormalX=0 NormalY=0 NormalZ=1 AngleXU=0 Radius=1
    g169: Circle CenterX=179.022 CenterY=120.221 CenterZ=0 NormalX=0 NormalY=0 NormalZ=1 AngleXU=0 Radius=1
    g170: BSplineCurve PolesCount=3 KnotsCount=2 Degree=2 IsPeriodic=0
    g171: GeomPoint X=175.022 Y=124.221 Z=0
    g172: GeomPoint X=179.022 Y=120.221 Z=0
    g173: Circle CenterX=62.0728 CenterY=124.221 CenterZ=0 NormalX=0 NormalY=0 NormalZ=1 AngleXU=0 Radius=1
    g174: Circle CenterX=58.0728 CenterY=124.221 CenterZ=0 NormalX=0 NormalY=0 NormalZ=1 AngleXU=0 Radius=1
    g175: Circle CenterX=61.1496 CenterY=121.665 CenterZ=0 NormalX=0 NormalY=0 NormalZ=1 AngleXU=0 Radius=1
    g176: BSplineCurve PolesCount=3 KnotsCount=2 Degree=2 IsPeriodic=0
    g177: GeomPoint X=62.0728 Y=124.221 Z=0
    g178: GeomPoint X=61.1496 Y=121.665 Z=0
    g179: LineSegment StartX=62.0728 StartY=124.221 StartZ=0 EndX=175.022 EndY=124.221 EndZ=0
    g180: LineSegment StartX=179.022 StartY=120.221 StartZ=0 EndX=179.022 EndY=27.0628 EndZ=0
    g181: LineSegment StartX=185.124 StartY=27.0628 StartZ=0 EndX=185.124 EndY=120.221 EndZ=0
    g182: LineSegment StartX=189.124 StartY=124.221 StartZ=0 EndX=302.073 EndY=124.221 EndZ=0
    g183: LineSegment StartX=302.996 StartY=121.665 StartZ=0 EndX=189.124 EndY=27.0628 EndZ=0
    g184: LineSegment StartX=175.022 StartY=27.0628 StartZ=0 EndX=61.1496 EndY=121.665 EndZ=0
    g185: Circle CenterX=61.5791 CenterY=75.4095 CenterZ=0 NormalX=0 NormalY=0 NormalZ=1 AngleXU=0 Radius=1
    g186: Circle CenterX=58.0728 CenterY=77.3346 CenterZ=0 NormalX=0 NormalY=0 NormalZ=1 AngleXU=0 Radius=1
    g187: Circle CenterX=58.0728 CenterY=73.3346 CenterZ=0 NormalX=0 NormalY=0 NormalZ=1 AngleXU=0 Radius=1
    g188: BSplineCurve PolesCount=3 KnotsCount=2 Degree=2 IsPeriodic=0
    g189: GeomPoint X=61.5791 Y=75.4095 Z=0
    g190: GeomPoint X=58.0728 Y=73.3346 Z=0
    g191: Circle CenterX=58.0728 CenterY=-40.8935 CenterZ=0 NormalX=0 NormalY=0 NormalZ=1 AngleXU=0 Radius=1
    g192: Circle CenterX=58.0728 CenterY=-44.8935 CenterZ=0 NormalX=0 NormalY=0 NormalZ=1 AngleXU=0 Radius=1
    g193: Circle CenterX=61.5791 CenterY=-42.9683 CenterZ=0 NormalX=0 NormalY=0 NormalZ=1 AngleXU=0 Radius=1
    g194: BSplineCurve PolesCount=3 KnotsCount=2 Degree=2 IsPeriodic=0
    g195: GeomPoint X=58.0728 Y=-40.8935 Z=0
    g196: GeomPoint X=61.5791 Y=-42.9683 Z=0
    g197: LineSegment StartX=61.5791 StartY=-42.9683 StartZ=0 EndX=165.871 EndY=14.2954 EndZ=0
    g198: LineSegment StartX=165.871 StartY=18.1458 StartZ=0 EndX=61.5791 EndY=75.4095 EndZ=0
    g199: LineSegment StartX=58.0728 StartY=73.3346 StartZ=0 EndX=58.0728 EndY=-40.8935 EndZ=0
    g200: Circle CenterX=302.567 CenterY=-42.9683 CenterZ=0 NormalX=0 NormalY=0 NormalZ=1 AngleXU=0 Radius=1
    g201: Circle CenterX=306.073 CenterY=-44.8935 CenterZ=0 NormalX=0 NormalY=0 NormalZ=1 AngleXU=0 Radius=1
    g202: Circle CenterX=306.073 CenterY=-40.8935 CenterZ=0 NormalX=0 NormalY=0 NormalZ=1 AngleXU=0 Radius=1
    g203: BSplineCurve PolesCount=3 KnotsCount=2 Degree=2 IsPeriodic=0
    g204: GeomPoint X=302.567 Y=-42.9683 Z=0
    g205: GeomPoint X=306.073 Y=-40.8935 Z=0
    g206: Circle CenterX=306.073 CenterY=73.3346 CenterZ=0 NormalX=0 NormalY=0 NormalZ=1 AngleXU=0 Radius=1
    g207: Circle CenterX=306.073 CenterY=77.3346 CenterZ=0 NormalX=0 NormalY=0 NormalZ=1 AngleXU=0 Radius=1
    g208: Circle CenterX=302.567 CenterY=75.4095 CenterZ=0 NormalX=0 NormalY=0 NormalZ=1 AngleXU=0 Radius=1
    g209: BSplineCurve PolesCount=3 KnotsCount=2 Degree=2 IsPeriodic=0
    g210: GeomPoint X=306.073 Y=73.3346 Z=0
    g211: GeomPoint X=302.567 Y=75.4095 Z=0
    g212: LineSegment StartX=302.567 StartY=-42.9683 StartZ=0 EndX=198.275 EndY=14.2954 EndZ=0
    g213: LineSegment StartX=198.275 StartY=18.1458 StartZ=0 EndX=302.567 EndY=75.4095 EndZ=0
    g214: LineSegment StartX=306.073 StartY=73.3346 StartZ=0 EndX=306.073 EndY=-40.8935 EndZ=0
    g215: LineSegment StartX=322.073 StartY=105.865 StartZ=0 EndX=328.643 EndY=105.865 EndZ=0
    g216: LineSegment StartX=318.073 StartY=120.221 StartZ=0 EndX=318.073 EndY=109.865 EndZ=0
    g217: LineSegment StartX=336.157 StartY=107.779 StartZ=0 EndX=362.567 EndY=122.294 EndZ=0
    g218: Circle CenterX=362.073 CenterY=124.221 CenterZ=0 NormalX=0 NormalY=0 NormalZ=1 AngleXU=0 Radius=1
    g219: Circle CenterX=366.073 CenterY=124.221 CenterZ=0 NormalX=0 NormalY=0 NormalZ=1 AngleXU=0 Radius=1
    g220: Circle CenterX=362.567 CenterY=122.294 CenterZ=0 NormalX=0 NormalY=0 NormalZ=1 AngleXU=0 Radius=1
    g221: BSplineCurve PolesCount=3 KnotsCount=2 Degree=2 IsPeriodic=0
    g222: GeomPoint X=362.073 Y=124.221 Z=0
    g223: GeomPoint X=362.567 Y=122.294 Z=0
    g224: Circle CenterX=322.073 CenterY=124.221 CenterZ=0 NormalX=0 NormalY=0 NormalZ=1 AngleXU=0 Radius=1
    g225: Circle CenterX=318.073 CenterY=124.221 CenterZ=0 NormalX=0 NormalY=0 NormalZ=1 AngleXU=0 Radius=1
    g226: Circle CenterX=318.073 CenterY=120.221 CenterZ=0 NormalX=0 NormalY=0 NormalZ=1 AngleXU=0 Radius=1
    g227: BSplineCurve PolesCount=3 KnotsCount=2 Degree=2 IsPeriodic=0
    g228: GeomPoint X=322.073 Y=124.221 Z=0
    g229: GeomPoint X=318.073 Y=120.221 Z=0
    g230: Circle CenterX=322.073 CenterY=105.865 CenterZ=0 NormalX=0 NormalY=0 NormalZ=1 AngleXU=0 Radius=1
    g231: Circle CenterX=318.073 CenterY=105.865 CenterZ=0 NormalX=0 NormalY=0 NormalZ=1 AngleXU=0 Radius=1
    g232: Circle CenterX=318.073 CenterY=109.865 CenterZ=0 NormalX=0 NormalY=0 NormalZ=1 AngleXU=0 Radius=1
    g233: BSplineCurve PolesCount=3 KnotsCount=2 Degree=2 IsPeriodic=0
    g234: GeomPoint X=322.073 Y=105.865 Z=0
    g235: GeomPoint X=318.073 Y=109.865 Z=0
    g236: Circle CenterX=336.157 CenterY=107.779 CenterZ=0 NormalX=0 NormalY=0 NormalZ=1 AngleXU=0 Radius=1
    g237: Circle CenterX=332.651 CenterY=105.853 CenterZ=0 NormalX=0 NormalY=0 NormalZ=1 AngleXU=0 Radius=1
    g238: Circle CenterX=328.643 CenterY=105.865 CenterZ=0 NormalX=0 NormalY=0 NormalZ=1 AngleXU=0 Radius=1
    g239: BSplineCurve PolesCount=3 KnotsCount=2 Degree=2 IsPeriodic=0
    g240: GeomPoint X=336.157 Y=107.779 Z=0
    g241: GeomPoint X=328.643 Y=105.865 Z=0
    g242: LineSegment StartX=322.073 StartY=124.221 StartZ=0 EndX=362.073 EndY=124.221 EndZ=0
    g243: Circle CenterX=371.567 CenterY=-80.8644 CenterZ=0 NormalX=0 NormalY=0 NormalZ=1 AngleXU=0 Radius=1
    g244: Circle CenterX=375.073 CenterY=-82.7896 CenterZ=0 NormalX=0 NormalY=0 NormalZ=1 AngleXU=0 Radius=1
    g245: Circle CenterX=375.073 CenterY=-78.7896 CenterZ=0 NormalX=0 NormalY=0 NormalZ=1 AngleXU=0 Radius=1
    g246: BSplineCurve PolesCount=3 KnotsCount=2 Degree=2 IsPeriodic=0
    g247: GeomPoint X=371.567 Y=-80.8644 Z=0
    g248: GeomPoint X=375.073 Y=-78.7896 Z=0
    g249: Circle CenterX=321.579 CenterY=-53.4075 CenterZ=0 NormalX=0 NormalY=0 NormalZ=1 AngleXU=0 Radius=1
    g250: Circle CenterX=318.073 CenterY=-51.4823 CenterZ=0 NormalX=0 NormalY=0 NormalZ=1 AngleXU=0 Radius=1
    g251: Circle CenterX=318.073 CenterY=-47.4805 CenterZ=0 NormalX=0 NormalY=0 NormalZ=1 AngleXU=0 Radius=1
    g252: BSplineCurve PolesCount=3 KnotsCount=2 Degree=2 IsPeriodic=0
    g253: GeomPoint X=321.579 Y=-53.4075 Z=0
    g254: GeomPoint X=318.073 Y=-47.4805 Z=0
    g255: LineSegment StartX=371.567 StartY=-80.8644 StartZ=0 EndX=321.579 EndY=-53.4075 EndZ=0
    g256: Circle CenterX=321.579 CenterY=-67.3492 CenterZ=0 NormalX=0 NormalY=0 NormalZ=1 AngleXU=0 Radius=1
    g257: Circle CenterX=318.073 CenterY=-65.424 CenterZ=0 NormalX=0 NormalY=0 NormalZ=1 AngleXU=0 Radius=1
    g258: Circle CenterX=318.073 CenterY=-69.424 CenterZ=0 NormalX=0 NormalY=0 NormalZ=1 AngleXU=0 Radius=1
    g259: BSplineCurve PolesCount=3 KnotsCount=2 Degree=2 IsPeriodic=0
    g260: GeomPoint X=321.579 Y=-67.3492 Z=0
    g261: GeomPoint X=318.073 Y=-69.424 Z=0
    g262: Circle CenterX=362.567 CenterY=-89.8542 CenterZ=0 NormalX=0 NormalY=0 NormalZ=1 AngleXU=0 Radius=1
    g263: Circle CenterX=366.073 CenterY=-91.7794 CenterZ=0 NormalX=0 NormalY=0 NormalZ=1 AngleXU=0 Radius=1
    g264: Circle CenterX=362.073 CenterY=-91.7794 CenterZ=0 NormalX=0 NormalY=0 NormalZ=1 AngleXU=0 Radius=1
    g265: BSplineCurve PolesCount=3 KnotsCount=2 Degree=2 IsPeriodic=0
    g266: GeomPoint X=362.567 Y=-89.8542 Z=0
    g267: GeomPoint X=362.073 Y=-91.7794 Z=0
    g268: Circle CenterX=322.073 CenterY=-91.7794 CenterZ=0 NormalX=0 NormalY=0 NormalZ=1 AngleXU=0 Radius=1
    g269: Circle CenterX=318.073 CenterY=-91.7794 CenterZ=0 NormalX=0 NormalY=0 NormalZ=1 AngleXU=0 Radius=1
    g270: Circle CenterX=318.073 CenterY=-87.7794 CenterZ=0 NormalX=0 NormalY=0 NormalZ=1 AngleXU=0 Radius=1
    g271: BSplineCurve PolesCount=3 KnotsCount=2 Degree=2 IsPeriodic=0
    g272: GeomPoint X=322.073 Y=-91.7794 Z=0
    g273: GeomPoint X=318.073 Y=-87.7794 Z=0
    g274: LineSegment StartX=362.567 StartY=-89.8542 StartZ=0 EndX=321.579 EndY=-67.3492 EndZ=0
    g275: LineSegment StartX=318.073 StartY=-69.424 StartZ=0 EndX=318.073 EndY=-87.7794 EndZ=0
    g276: LineSegment StartX=322.073 StartY=-91.7794 StartZ=0 EndX=362.073 EndY=-91.7794 EndZ=0
    g277: Circle CenterX=2.07281 CenterY=124.221 CenterZ=0 NormalX=0 NormalY=0 NormalZ=1 AngleXU=0 Radius=1
    g278: Circle CenterX=1.57905 CenterY=122.295 CenterZ=0 NormalX=0 NormalY=0 NormalZ=1 AngleXU=0 Radius=1
    g279: BSplineCurve PolesCount=3 KnotsCount=2 Degree=2 IsPeriodic=0
    g280: GeomPoint X=2.07281 Y=124.221 Z=0
    g281: GeomPoint X=1.57905 Y=122.295 Z=0
    g282: Circle CenterX=42.0728 CenterY=124.221 CenterZ=0 NormalX=0 NormalY=0 NormalZ=1 AngleXU=0 Radius=1
    g283: Circle CenterX=46.0728 CenterY=124.221 CenterZ=0 NormalX=0 NormalY=0 NormalZ=1 AngleXU=0 Radius=1
    g284: Circle CenterX=46.0728 CenterY=120.221 CenterZ=0 NormalX=0 NormalY=0 NormalZ=1 AngleXU=0 Radius=1
    g285: BSplineCurve PolesCount=3 KnotsCount=2 Degree=2 IsPeriodic=0
    g286: GeomPoint X=42.0728 Y=124.221 Z=0
    g287: GeomPoint X=46.0728 Y=120.221 Z=0
    g288: Circle CenterX=46.0728 CenterY=109.865 CenterZ=0 NormalX=0 NormalY=0 NormalZ=1 AngleXU=0 Radius=1
    g289: Circle CenterX=46.0728 CenterY=105.865 CenterZ=0 NormalX=0 NormalY=0 NormalZ=1 AngleXU=0 Radius=1
    g290: Circle CenterX=42.0728 CenterY=105.865 CenterZ=0 NormalX=0 NormalY=0 NormalZ=1 AngleXU=0 Radius=1
    g291: BSplineCurve PolesCount=3 KnotsCount=2 Degree=2 IsPeriodic=0
    g292: GeomPoint X=46.0728 Y=109.865 Z=0
    g293: GeomPoint X=42.0728 Y=105.865 Z=0
    g294: Circle CenterX=35.5028 CenterY=105.865 CenterZ=0 NormalX=0 NormalY=0 NormalZ=1 AngleXU=0 Radius=1
    g295: Circle CenterX=31.5028 CenterY=105.865 CenterZ=0 NormalX=0 NormalY=0 NormalZ=1 AngleXU=0 Radius=1
    g296: Circle CenterX=27.9965 CenterY=107.79 CenterZ=0 NormalX=0 NormalY=0 NormalZ=1 AngleXU=0 Radius=1
    g297: BSplineCurve PolesCount=3 KnotsCount=2 Degree=2 IsPeriodic=0
    g298: GeomPoint X=35.5028 Y=105.865 Z=0
    g299: GeomPoint X=27.9965 Y=107.79 Z=0
    g300: LineSegment StartX=2.07281 StartY=124.221 StartZ=0 EndX=42.0728 EndY=124.221 EndZ=0
    g301: LineSegment StartX=46.0728 StartY=120.221 StartZ=0 EndX=46.0728 EndY=109.865 EndZ=0
    g302: LineSegment StartX=42.0728 StartY=105.865 StartZ=0 EndX=35.5028 EndY=105.865 EndZ=0
    g303: LineSegment StartX=27.9965 StartY=107.79 StartZ=0 EndX=1.57905 EndY=122.295 EndZ=0
    g304: Circle CenterX=42.5666 CenterY=-67.3492 CenterZ=0 NormalX=0 NormalY=0 NormalZ=1 AngleXU=0 Radius=1
    g305: Circle CenterX=46.0728 CenterY=-65.424 CenterZ=0 NormalX=0 NormalY=0 NormalZ=1 AngleXU=0 Radius=1
    g306: Circle CenterX=46.0728 CenterY=-69.424 CenterZ=0 NormalX=0 NormalY=0 NormalZ=1 AngleXU=0 Radius=1
    g307: BSplineCurve PolesCount=3 KnotsCount=2 Degree=2 IsPeriodic=0
    g308: GeomPoint X=42.5666 Y=-67.3492 Z=0
    g309: GeomPoint X=46.0728 Y=-69.424 Z=0
    g310: Circle CenterX=46.0728 CenterY=-87.7794 CenterZ=0 NormalX=0 NormalY=0 NormalZ=1 AngleXU=0 Radius=1
    g311: Circle CenterX=46.0728 CenterY=-91.7794 CenterZ=0 NormalX=0 NormalY=0 NormalZ=1 AngleXU=0 Radius=1
    g312: Circle CenterX=42.0728 CenterY=-91.7794 CenterZ=0 NormalX=0 NormalY=0 NormalZ=1 AngleXU=0 Radius=1
    g313: BSplineCurve PolesCount=3 KnotsCount=2 Degree=2 IsPeriodic=0
    g314: GeomPoint X=46.0728 Y=-87.7794 Z=0
    g315: GeomPoint X=42.0728 Y=-91.7794 Z=0
    g316: Circle CenterX=2.07281 CenterY=-91.7794 CenterZ=0 NormalX=0 NormalY=0 NormalZ=1 AngleXU=0 Radius=1
    g317: Circle CenterX=-1.92719 CenterY=-91.7794 CenterZ=0 NormalX=0 NormalY=0 NormalZ=1 AngleXU=0 Radius=1
    g318: Circle CenterX=1.57905 CenterY=-89.8542 CenterZ=0 NormalX=0 NormalY=0 NormalZ=1 AngleXU=0 Radius=1
    g319: BSplineCurve PolesCount=3 KnotsCount=2 Degree=2 IsPeriodic=0
    g320: GeomPoint X=2.07281 Y=-91.7794 Z=0
    g321: GeomPoint X=1.57905 Y=-89.8542 Z=0
    g322: LineSegment StartX=2.07281 StartY=-91.7794 StartZ=0 EndX=42.0728 EndY=-91.7794 EndZ=0
    g323: LineSegment StartX=46.0728 StartY=-87.7794 StartZ=0 EndX=46.0728 EndY=-69.424 EndZ=0
    g324: LineSegment StartX=42.5666 StartY=-67.3492 StartZ=0 EndX=1.57905 EndY=-89.8542 EndZ=0
    g325: Circle CenterX=322.073 CenterY=76.4095 CenterZ=0 NormalX=0 NormalY=0 NormalZ=1 AngleXU=0 Radius=4
    g326: BSplineCurve PolesCount=3 KnotsCount=2 Degree=2 IsPeriodic=0
    g327: GeomPoint X=318.073 Y=72.4095 Z=0
    g328: GeomPoint X=322.073 Y=76.4095 Z=0
    g329: Circle CenterX=375.073 CenterY=72.4095 CenterZ=0 NormalX=0 NormalY=0 NormalZ=1 AngleXU=0 Radius=1
    g330: Circle CenterX=375.073 CenterY=76.4095 CenterZ=0 NormalX=0 NormalY=0 NormalZ=1 AngleXU=0 Radius=1
    g331: Circle CenterX=371.073 CenterY=76.4095 CenterZ=0 NormalX=0 NormalY=0 NormalZ=1 AngleXU=0 Radius=1
    g332: BSplineCurve PolesCount=3 KnotsCount=2 Degree=2 IsPeriodic=0
    g333: GeomPoint X=375.073 Y=72.4095 Z=0
    g334: GeomPoint X=371.073 Y=76.4095 Z=0
    g335: LineSegment StartX=322.073 StartY=76.4095 StartZ=0 EndX=371.073 EndY=76.4095 EndZ=0
    g336: LineSegment StartX=318.073 StartY=72.4095 StartZ=0 EndX=318.073 EndY=-47.4805 EndZ=0
    g337: LineSegment StartX=375.073 StartY=72.4095 StartZ=0 EndX=375.073 EndY=-78.7896 EndZ=0
    g338: ArcOfCircle CenterX=-26.9272 CenterY=22.1087 CenterZ=0 NormalX=0 NormalY=0 NormalZ=1 AngleXU=0 Radius=4 StartAngle=5e-16 EndAngle=3.14159
    g339: LineSegment StartX=-22.9272 StartY=22.1087 StartZ=0 EndX=-18.9272 EndY=-83.7794 EndZ=0
    g340: LineSegment StartX=-34.9272 StartY=-83.7794 StartZ=0 EndX=-30.9272 EndY=22.1087 EndZ=0
    g341: ArcOfCircle CenterX=391.073 CenterY=22.1087 CenterZ=0 NormalX=0 NormalY=0 NormalZ=1 AngleXU=0 Radius=4 StartAngle=0 EndAngle=3.14159
    g342: LineSegment StartX=387.073 StartY=22.1087 StartZ=0 EndX=383.073 EndY=-83.7794 EndZ=0
    g343: LineSegment StartX=395.073 StartY=22.1087 StartZ=0 EndX=399.073 EndY=-83.7794 EndZ=0
    g344: Circle CenterX=-10.9272 CenterY=-78.7794 CenterZ=0 NormalX=0 NormalY=0 NormalZ=1 AngleXU=0 Radius=1
    g345: Circle CenterX=-10.9272 CenterY=-82.7794 CenterZ=0 NormalX=0 NormalY=0 NormalZ=1 AngleXU=0 Radius=1
    g346: Circle CenterX=-7.42095 CenterY=-80.8542 CenterZ=0 NormalX=0 NormalY=0 NormalZ=1 AngleXU=0 Radius=1
    g347: BSplineCurve PolesCount=3 KnotsCount=2 Degree=2 IsPeriodic=0
    g348: GeomPoint X=-10.9272 Y=-78.7794 Z=0
    g349: GeomPoint X=-7.42095 Y=-80.8542 Z=0
    g350: Circle CenterX=42.5666 CenterY=-53.4075 CenterZ=0 NormalX=0 NormalY=0 NormalZ=1 AngleXU=0 Radius=1
    g351: Circle CenterX=46.0728 CenterY=-51.4823 CenterZ=0 NormalX=0 NormalY=0 NormalZ=1 AngleXU=0 Radius=1
    g352: Circle CenterX=46.0728 CenterY=-47.4823 CenterZ=0 NormalX=0 NormalY=0 NormalZ=1 AngleXU=0 Radius=1
    g353: BSplineCurve PolesCount=3 KnotsCount=2 Degree=2 IsPeriodic=0
    g354: GeomPoint X=42.5666 Y=-53.4075 Z=0
    g355: GeomPoint X=46.0728 Y=-47.4823 Z=0
    g356: Circle CenterX=46.0728 CenterY=72.4095 CenterZ=0 NormalX=0 NormalY=0 NormalZ=1 AngleXU=0 Radius=1
    g357: Circle CenterX=46.0728 CenterY=76.4095 CenterZ=0 NormalX=0 NormalY=0 NormalZ=1 AngleXU=0 Radius=1
    g358: Circle CenterX=42.0728 CenterY=76.4095 CenterZ=0 NormalX=0 NormalY=0 NormalZ=1 AngleXU=0 Radius=1
    g359: BSplineCurve PolesCount=3 KnotsCount=2 Degree=2 IsPeriodic=0
    g360: GeomPoint X=46.0728 Y=72.4095 Z=0
    g361: GeomPoint X=42.0728 Y=76.4095 Z=0
    g362: Circle CenterX=-6.92718 CenterY=76.4095 CenterZ=0 NormalX=0 NormalY=0 NormalZ=1 AngleXU=0 Radius=1
    g363: Circle CenterX=-10.9272 CenterY=76.4095 CenterZ=0 NormalX=0 NormalY=0 NormalZ=1 AngleXU=0 Radius=1
    g364: Circle CenterX=-10.9272 CenterY=72.4095 CenterZ=0 NormalX=0 NormalY=0 NormalZ=1 AngleXU=0 Radius=1
    g365: BSplineCurve PolesCount=3 KnotsCount=2 Degree=2 IsPeriodic=0
    g366: GeomPoint X=-6.92718 Y=76.4095 Z=0
    g367: GeomPoint X=-10.9272 Y=72.4095 Z=0
    g368: LineSegment StartX=-10.9272 StartY=72.4095 StartZ=0 EndX=-10.9272 EndY=-78.7794 EndZ=0
    g369: LineSegment StartX=-7.42095 StartY=-80.8542 StartZ=0 EndX=42.5666 EndY=-53.4075 EndZ=0
    g370: LineSegment StartX=46.0728 StartY=-47.4823 StartZ=0 EndX=46.0728 EndY=72.4095 EndZ=0
    g371: LineSegment StartX=42.0728 StartY=76.4095 StartZ=0 EndX=-6.92719 EndY=76.4095 EndZ=0
    g372: LineSegment StartX=232.072 StartY=136.221 StartZ=0 EndX=232.072 EndY=-117.815 EndZ=0
    g373: LineSegment StartX=132.072 StartY=136.221 StartZ=0 EndX=132.072 EndY=-121.309 EndZ=0
    g374: LineSegment StartX=245.072 StartY=136.221 StartZ=0 EndX=245.072 EndY=-116.499 EndZ=0
    g375: LineSegment StartX=119.072 StartY=136.221 StartZ=0 EndX=119.072 EndY=-116.228 EndZ=0
    g376: LineSegment StartX=-42.9272 StartY=136.221 StartZ=0 EndX=407.073 EndY=136.221 EndZ=0
  constraints (623):
    c: Vertical(g0)
    c: Vertical(g1)
    c: Block(g1)
    c: Block(g0)
    c: Weight(g4) = 1
    c: Equal(g4,g5)
    c: Equal(g4,g6)
    c: InternalAlignment(g4,g7)
    c: InternalAlignment(g5,g7)
    c: InternalAlignment(g6,g7)
    c: InternalAlignment(g8,g7)
    c: InternalAlignment(g9,g7)
    c: Weight(g10) = 1
    c: Equal(g10,g11)
    c: Equal(g10,g12)
    c: InternalAlignment(g10,g13)
    c: InternalAlignment(g11,g13)
    c: InternalAlignment(g12,g13)
    c: InternalAlignment(g14,g13)
    c: InternalAlignment(g15,g13)
    c: Block(g13)
    c: Block(g7)
    c: Weight(g16) = 1
    c: Equal(g16,g17)
    c: Equal(g16,g18)
    c: InternalAlignment(g16,g19)
    c: InternalAlignment(g17,g19)
    c: InternalAlignment(g18,g19)
    c: InternalAlignment(g20,g19)
    c: InternalAlignment(g21,g19)
    c: Weight(g22) = 1
    c: Equal(g22,g23)
    c: Equal(g22,g24)
    c: InternalAlignment(g22,g25)
    c: InternalAlignment(g23,g25)
    c: InternalAlignment(g24,g25)
    c: InternalAlignment(g26,g25)
    c: InternalAlignment(g27,g25)
    c: Block(g25)
    c: Block(g19)
    c: Weight(g28) = 1
    c: Equal(g28,g29)
    c: Equal(g28,g30)
    c: InternalAlignment(g28,g31)
    c: InternalAlignment(g29,g31)
    c: InternalAlignment(g30,g31)
    c: InternalAlignment(g32,g31)
    c: InternalAlignment(g33,g31)
    c: Weight(g34) = 1
    c: Equal(g34,g35)
    c: Equal(g34,g36)
    c: InternalAlignment(g34,g37)
    c: InternalAlignment(g35,g37)
    c: InternalAlignment(g36,g37)
    c: InternalAlignment(g38,g37)
    c: InternalAlignment(g39,g37)
    c: Block(g31)
    c: Block(g37)
    c: Coincident(g40,g1)
    c: Coincident(g40,g0)
    c: Horizontal(g40)
    c: Distance(g40) = 450
    c: Weight(g41) = 1
    c: Equal(g41,g42)
    c: Equal(g41,g43)
    c: InternalAlignment(g41,g44)
    c: InternalAlignment(g42,g44)
    c: InternalAlignment(g43,g44)
    c: InternalAlignment(g45,g44)
    c: InternalAlignment(g46,g44)
    c: Block(g44)
    c: Weight(g47) = 1
    c: Equal(g47,g48)
    c: Equal(g47,g49)
    c: InternalAlignment(g47,g50)
    c: InternalAlignment(g48,g50)
    c: InternalAlignment(g49,g50)
    c: InternalAlignment(g51,g50)
    c: InternalAlignment(g52,g50)
    c: Block(g50)
    c: Weight(g53) = 1
    c: Equal(g53,g54)
    c: Equal(g53,g55)
    c: InternalAlignment(g53,g56)
    c: InternalAlignment(g54,g56)
    c: InternalAlignment(g55,g56)
    c: InternalAlignment(g57,g56)
    c: InternalAlignment(g58,g56)
    c: Block(g56)
    c: Weight(g59) = 1
    c: Equal(g59,g60)
    c: Equal(g59,g61)
    c: InternalAlignment(g59,g62)
    c: InternalAlignment(g60,g62)
    c: InternalAlignment(g61,g62)
    c: InternalAlignment(g63,g62)
    c: InternalAlignment(g64,g62)
    c: Block(g62)
    c: Weight(g65) = 1
    c: Equal(g65,g66)
    c: Equal(g65,g67)
    c: InternalAlignment(g65,g68)
    c: InternalAlignment(g66,g68)
    c: InternalAlignment(g67,g68)
    c: InternalAlignment(g69,g68)
    c: InternalAlignment(g70,g68)
    c: Weight(g71) = 1
    c: Equal(g71,g72)
    c: Equal(g71,g73)
    c: InternalAlignment(g71,g74)
    c: InternalAlignment(g72,g74)
    c: InternalAlignment(g73,g74)
    c: InternalAlignment(g75,g74)
    c: InternalAlignment(g76,g74)
    c: Block(g68)
    c: Block(g74)
    c: Coincident(g77,g68)
    c: Coincident(g77,g74)
    c: Vertical(g77)
    c: Coincident(g78,g68)
    c: Coincident(g78,g50)
    c: Coincident(g79,g50)
    c: Coincident(g79,g74)
    c: Weight(g80) = 1
    c: Equal(g80,g81)
    c: Equal(g80,g82)
    c: InternalAlignment(g80,g83)
    c: InternalAlignment(g81,g83)
    c: InternalAlignment(g82,g83)
    c: InternalAlignment(g84,g83)
    c: InternalAlignment(g85,g83)
    c: Weight(g86) = 1
    c: Equal(g86,g87)
    c: Equal(g86,g88)
    c: InternalAlignment(g86,g89)
    c: InternalAlignment(g87,g89)
    c: InternalAlignment(g88,g89)
    c: InternalAlignment(g90,g89)
    c: InternalAlignment(g91,g89)
    c: Block(g83)
    c: Block(g89)
    c: Coincident(g92,g83)
    c: Coincident(g92,g89)
    c: Vertical(g92)
    c: Coincident(g93,g83)
    c: Coincident(g93,g44)
    c: Coincident(g94,g44)
    c: Coincident(g94,g89)
    c: Weight(g95) = 1
    c: Equal(g95,g96)
    c: Equal(g95,g97)
    c: InternalAlignment(g95,g98)
    c: InternalAlignment(g96,g98)
    c: InternalAlignment(g97,g98)
    c: InternalAlignment(g99,g98)
    c: InternalAlignment(g100,g98)
    c: Weight(g101) = 1
    c: Equal(g101,g102)
    c: Equal(g101,g103)
    c: InternalAlignment(g101,g104)
    c: InternalAlignment(g102,g104)
    c: InternalAlignment(g103,g104)
    c: InternalAlignment(g105,g104)
    c: InternalAlignment(g106,g104)
    c: Block(g98)
    c: Block(g104)
    c: Coincident(g107,g98)
    c: Coincident(g107,g104)
    c: Vertical(g107)
    c: Coincident(g108,g104)
    c: Coincident(g108,g62)
    c: Coincident(g109,g62)
    c: Coincident(g109,g98)
    c: Weight(g110) = 1
    c: Equal(g110,g111)
    c: Equal(g110,g112)
    c: InternalAlignment(g110,g113)
    c: InternalAlignment(g111,g113)
    c: InternalAlignment(g112,g113)
    c: InternalAlignment(g114,g113)
    c: InternalAlignment(g115,g113)
    c: Weight(g116) = 1
    c: Equal(g116,g117)
    c: Equal(g116,g118)
    c: InternalAlignment(g116,g119)
    c: InternalAlignment(g117,g119)
    c: InternalAlignment(g118,g119)
    c: InternalAlignment(g120,g119)
    c: InternalAlignment(g121,g119)
    c: Block(g113)
    c: Block(g119)
    c: Coincident(g122,g113)
    c: Coincident(g122,g119)
    c: Vertical(g122)
    c: Coincident(g123,g119)
    c: Coincident(g123,g56)
    c: Coincident(g124,g56)
    c: Coincident(g124,g113)
    c: Weight(g125) = 1
    c: Equal(g125,g126)
    c: Equal(g125,g127)
    c: InternalAlignment(g125,g128)
    c: InternalAlignment(g126,g128)
    c: InternalAlignment(g127,g128)
    c: InternalAlignment(g129,g128)
    c: InternalAlignment(g130,g128)
    c: Weight(g131) = 1
    c: Equal(g131,g132)
    c: Equal(g131,g133)
    c: InternalAlignment(g131,g134)
    c: InternalAlignment(g132,g134)
    c: InternalAlignment(g133,g134)
    c: InternalAlignment(g135,g134)
    c: InternalAlignment(g136,g134)
    c: Weight(g137) = 1
    c: Equal(g137,g138)
    c: Equal(g137,g139)
    c: InternalAlignment(g137,g140)
    c: InternalAlignment(g138,g140)
    c: InternalAlignment(g139,g140)
    c: InternalAlignment(g141,g140)
    c: InternalAlignment(g142,g140)
    c: Weight(g143) = 1
    c: Equal(g143,g144)
    c: Equal(g143,g145)
    c: InternalAlignment(g143,g146)
    c: InternalAlignment(g144,g146)
    c: InternalAlignment(g145,g146)
    c: InternalAlignment(g147,g146)
    c: InternalAlignment(g148,g146)
    c: Block(g146)
    c: Block(g140)
    c: Block(g134)
    c: Block(g128)
    c: Coincident(g149,g25)
    c: Coincident(g149,g146)
    c: Coincident(g150,g146)
    c: Coincident(g150,g140)
    c: Horizontal(g150)
    c: Coincident(g151,g140)
    c: Coincident(g151,g25)
    c: Vertical(g151)
    c: Coincident(g152,g19)
    c: Coincident(g152,g134)
    c: Vertical(g152)
    c: Coincident(g153,g134)
    c: Coincident(g153,g128)
    c: Horizontal(g153)
    c: Coincident(g154,g128)
    c: Coincident(g154,g19)
    c: Weight(g155) = 1
    c: Equal(g155,g156)
    c: Equal(g155,g157)
    c: InternalAlignment(g155,g158)
    c: InternalAlignment(g156,g158)
    c: InternalAlignment(g157,g158)
    c: InternalAlignment(g159,g158)
    c: InternalAlignment(g160,g158)
    c: Weight(g161) = 1
    c: Equal(g161,g162)
    c: Equal(g161,g163)
    c: InternalAlignment(g161,g164)
    c: InternalAlignment(g162,g164)
    c: InternalAlignment(g163,g164)
    c: InternalAlignment(g165,g164)
    c: InternalAlignment(g166,g164)
    c: Weight(g167) = 1
    c: Equal(g167,g168)
    c: Equal(g167,g169)
    c: InternalAlignment(g167,g170)
    c: InternalAlignment(g168,g170)
    c: InternalAlignment(g169,g170)
    c: InternalAlignment(g171,g170)
    c: InternalAlignment(g172,g170)
    c: Weight(g173) = 1
    c: Equal(g173,g174)
    c: Equal(g173,g175)
    c: InternalAlignment(g173,g176)
    c: InternalAlignment(g174,g176)
    c: InternalAlignment(g175,g176)
    c: InternalAlignment(g177,g176)
    c: InternalAlignment(g178,g176)
    c: Block(g176)
    c: Block(g170)
    c: Block(g164)
    c: Block(g158)
    c: Coincident(g179,g176)
    c: Coincident(g179,g170)
    c: Horizontal(g179)
    c: Coincident(g180,g170)
    c: Coincident(g180,g7)
    c: Vertical(g180)
    c: Coincident(g181,g13)
    c: Coincident(g181,g164)
    c: Vertical(g181)
    c: Coincident(g182,g164)
    c: Coincident(g182,g158)
    c: Horizontal(g182)
    c: Coincident(g183,g158)
    c: Coincident(g183,g13)
    c: Coincident(g184,g7)
    c: Weight(g185) = 1
    c: Equal(g185,g186)
    c: Equal(g185,g187)
    c: InternalAlignment(g185,g188)
    c: InternalAlignment(g186,g188)
    c: InternalAlignment(g187,g188)
    c: InternalAlignment(g189,g188)
    c: InternalAlignment(g190,g188)
    c: Weight(g191) = 1
    c: Equal(g191,g192)
    c: Equal(g191,g193)
    c: InternalAlignment(g191,g194)
    c: InternalAlignment(g192,g194)
    c: InternalAlignment(g193,g194)
    c: InternalAlignment(g195,g194)
    c: InternalAlignment(g196,g194)
    c: Block(g194)
    c: Block(g188)
    c: Coincident(g197,g194)
    c: Coincident(g197,g31)
    c: Coincident(g198,g31)
    c: Coincident(g198,g188)
    c: Coincident(g199,g188)
    c: Coincident(g199,g194)
    c: Vertical(g199)
    c: Weight(g200) = 1
    c: Equal(g200,g201)
    c: Equal(g200,g202)
    c: InternalAlignment(g200,g203)
    c: InternalAlignment(g201,g203)
    c: InternalAlignment(g202,g203)
    c: InternalAlignment(g204,g203)
    c: InternalAlignment(g205,g203)
    c: Weight(g206) = 1
    c: Equal(g206,g207)
    c: Equal(g206,g208)
    c: InternalAlignment(g206,g209)
    c: InternalAlignment(g207,g209)
    c: InternalAlignment(g208,g209)
    c: InternalAlignment(g210,g209)
    c: InternalAlignment(g211,g209)
    c: Block(g209)
    c: Block(g203)
    c: Coincident(g212,g203)
    c: Coincident(g212,g37)
    c: Coincident(g213,g37)
    c: Coincident(g213,g209)
    c: Coincident(g214,g209)
    c: Coincident(g214,g203)
    c: Vertical(g214)
    c: Horizontal(g215)
    c: Block(g215)
    c: Vertical(g216)
    c: Block(g216)
    c: Block(g217)
    c: Weight(g218) = 1
    c: Equal(g218,g219)
    c: Equal(g218,g220)
    c: InternalAlignment(g218,g221)
    c: InternalAlignment(g219,g221)
    c: InternalAlignment(g220,g221)
    c: InternalAlignment(g222,g221)
    c: InternalAlignment(g223,g221)
    c: Weight(g224) = 1
    c: Equal(g224,g225)
    c: Equal(g224,g226)
    c: InternalAlignment(g224,g227)
    c: InternalAlignment(g225,g227)
    c: InternalAlignment(g226,g227)
    c: InternalAlignment(g228,g227)
    c: InternalAlignment(g229,g227)
    c: Weight(g230) = 1
    c: Equal(g230,g231)
    c: Equal(g230,g232)
    c: InternalAlignment(g230,g233)
    c: InternalAlignment(g231,g233)
    c: InternalAlignment(g232,g233)
    c: InternalAlignment(g234,g233)
    c: InternalAlignment(g235,g233)
    c: Weight(g236) = 1
    c: Equal(g236,g237)
    c: Equal(g236,g238)
    c: InternalAlignment(g236,g239)
    c: InternalAlignment(g237,g239)
    c: InternalAlignment(g238,g239)
    c: InternalAlignment(g240,g239)
    c: InternalAlignment(g241,g239)
    c: Block(g221)
    c: Block(g227)
    c: Block(g233)
    c: Block(g239)
    c: Coincident(g242,g227)
    c: Coincident(g242,g221)
    c: Horizontal(g242)
    c: Block(g184)
    c: Weight(g243) = 1
    c: Equal(g243,g244)
    c: Equal(g243,g245)
    c: InternalAlignment(g243,g246)
    c: InternalAlignment(g244,g246)
    c: InternalAlignment(g245,g246)
    c: InternalAlignment(g247,g246)
    c: InternalAlignment(g248,g246)
    c: Weight(g249) = 1
    c: Equal(g249,g250)
    c: Equal(g249,g251)
    c: InternalAlignment(g249,g252)
    c: InternalAlignment(g250,g252)
    c: InternalAlignment(g251,g252)
    c: InternalAlignment(g253,g252)
    c: InternalAlignment(g254,g252)
    c: Block(g246)
    c: Block(g252)
    c: Coincident(g255,g246)
    c: Coincident(g255,g252)
    c: Weight(g256) = 1
    c: Equal(g256,g257)
    c: Equal(g256,g258)
    c: InternalAlignment(g256,g259)
    c: InternalAlignment(g257,g259)
    c: InternalAlignment(g258,g259)
    c: InternalAlignment(g260,g259)
    c: InternalAlignment(g261,g259)
    c: Weight(g262) = 1
    c: Equal(g262,g263)
    c: Equal(g262,g264)
    c: InternalAlignment(g262,g265)
    c: InternalAlignment(g263,g265)
    c: InternalAlignment(g264,g265)
    c: InternalAlignment(g266,g265)
    c: InternalAlignment(g267,g265)
    c: Weight(g268) = 1
    c: Equal(g268,g269)
    c: Equal(g268,g270)
    c: InternalAlignment(g268,g271)
    c: InternalAlignment(g269,g271)
    c: InternalAlignment(g270,g271)
    c: InternalAlignment(g272,g271)
    c: InternalAlignment(g273,g271)
    c: Block(g271)
    c: Block(g265)
    c: Block(g259)
    c: Coincident(g274,g265)
    c: Coincident(g274,g259)
    c: Coincident(g275,g259)
    c: Coincident(g275,g271)
    c: Vertical(g275)
    c: Coincident(g276,g271)
    c: Coincident(g276,g265)
    c: Horizontal(g276)
    c: Weight(g277) = 1
    c: Equal(g277,g278)
    c: InternalAlignment(g277,g279)
    c: InternalAlignment(g278,g279)
    c: InternalAlignment(g280,g279)
    c: InternalAlignment(g281,g279)
    c: Weight(g282) = 1
    c: InternalAlignment(g283,g285)
    c: InternalAlignment(g284,g285)
    c: InternalAlignment(g286,g285)
    c: InternalAlignment(g287,g285)
    c: Weight(g288) = 1
    c: Equal(g288,g289)
    c: Equal(g288,g290)
    c: InternalAlignment(g288,g291)
    c: InternalAlignment(g289,g291)
    c: InternalAlignment(g290,g291)
    c: InternalAlignment(g292,g291)
    c: InternalAlignment(g293,g291)
    c: Equal(g294,g295)
    c: Equal(g294,g296)
    c: InternalAlignment(g294,g297)
    c: InternalAlignment(g295,g297)
    c: InternalAlignment(g296,g297)
    c: InternalAlignment(g298,g297)
    c: InternalAlignment(g299,g297)
    c: Block(g285)
    c: Block(g291)
    c: Block(g297)
    c: Block(g279)
    c: Coincident(g300,g279)
    c: Coincident(g300,g285)
    c: Horizontal(g300)
    c: Coincident(g301,g285)
    c: Coincident(g301,g291)
    c: Vertical(g301)
    c: Coincident(g302,g291)
    c: Coincident(g302,g297)
    c: Horizontal(g302)
    c: Coincident(g303,g297)
    c: Coincident(g303,g279)
    c: Weight(g304) = 1
    c: Equal(g304,g305)
    c: Equal(g304,g306)
    c: InternalAlignment(g304,g307)
    c: InternalAlignment(g305,g307)
    c: InternalAlignment(g306,g307)
    c: InternalAlignment(g308,g307)
    c: InternalAlignment(g309,g307)
    c: Weight(g310) = 1
    c: Equal(g310,g311)
    c: Equal(g310,g312)
    c: InternalAlignment(g310,g313)
    c: InternalAlignment(g311,g313)
    c: InternalAlignment(g312,g313)
    c: InternalAlignment(g314,g313)
    c: InternalAlignment(g315,g313)
    c: Weight(g316) = 1
    c: Equal(g316,g317)
    c: Equal(g316,g318)
    c: InternalAlignment(g316,g319)
    c: InternalAlignment(g317,g319)
    c: InternalAlignment(g318,g319)
    c: InternalAlignment(g320,g319)
    c: InternalAlignment(g321,g319)
    c: Block(g319)
    c: Block(g313)
    c: Block(g307)
    c: Coincident(g322,g319)
    c: Coincident(g322,g313)
    c: Horizontal(g322)
    c: Coincident(g323,g313)
    c: Coincident(g323,g307)
    c: Vertical(g323)
    c: Coincident(g324,g307)
    c: Coincident(g324,g319)
    c: InternalAlignment(g325,g326)
    c: InternalAlignment(g327,g326)
    c: InternalAlignment(g328,g326)
    c: Block(g326)
    c: Equal(g329,g330)
    c: Equal(g329,g331)
    c: InternalAlignment(g329,g332)
    c: InternalAlignment(g330,g332)
    c: InternalAlignment(g331,g332)
    c: InternalAlignment(g333,g332)
    c: InternalAlignment(g334,g332)
    c: Block(g332)
    c: Coincident(g335,g326)
    c: Horizontal(g335)
    c: Block(g335)
    c: Coincident(g336,g326)
    c: Coincident(g336,g252)
    c: Vertical(g336)
    c: Coincident(g337,g332)
    c: Coincident(g337,g246)
    c: Vertical(g337)
    c: Block(g338)
    c: Block(g2)
    c: Distance(g336) = 119.89
    c: Coincident(g339,g338)
    c: Coincident(g339,g2)
    c: Coincident(g340,g2)
    c: Coincident(g340,g338)
    c: Block(g3)
    c: Block(g341)
    c: Coincident(g342,g341)
    c: Coincident(g342,g3)
    c: Coincident(g343,g341)
    c: Coincident(g343,g3)
    c: Block(g343)
    c: Block(g342)
    c: Weight(g344) = 1
    c: Equal(g344,g345)
    c: Equal(g344,g346)
    c: InternalAlignment(g344,g347)
    c: InternalAlignment(g345,g347)
    c: InternalAlignment(g346,g347)
    c: InternalAlignment(g348,g347)
    c: InternalAlignment(g349,g347)
    c: Weight(g350) = 1
    c: Equal(g350,g351)
    c: Equal(g350,g352)
    c: InternalAlignment(g350,g353)
    c: InternalAlignment(g351,g353)
    c: InternalAlignment(g352,g353)
    c: InternalAlignment(g354,g353)
    c: InternalAlignment(g355,g353)
    c: Weight(g356) = 1
    c: Equal(g356,g357)
    c: Equal(g356,g358)
    c: InternalAlignment(g356,g359)
    c: InternalAlignment(g357,g359)
    c: InternalAlignment(g358,g359)
    c: InternalAlignment(g360,g359)
    c: InternalAlignment(g361,g359)
    c: Weight(g362) = 1
    c: Equal(g362,g363)
    c: Equal(g362,g364)
    c: InternalAlignment(g362,g365)
    c: InternalAlignment(g363,g365)
    c: InternalAlignment(g364,g365)
    c: InternalAlignment(g366,g365)
    c: InternalAlignment(g367,g365)
    c: Block(g365)
    c: Block(g359)
    c: Block(g353)
    c: Block(g347)
    c: Coincident(g368,g365)
    c: Coincident(g368,g347)
    c: Vertical(g368)
    c: Coincident(g369,g347)
    c: Coincident(g369,g353)
    c: Coincident(g370,g353)
    c: Coincident(g370,g359)
    c: Vertical(g370)
    c: Coincident(g371,g359)
    c: Coincident(g371,g365)
    c: Horizontal(g371)
    c: Vertical(g372)
    c: Vertical(g373)
    c: Vertical(g374)
    c: Vertical(g375)
    c: Coincident(g376,g0)
    c: Coincident(g376,g1)
    c: Horizontal(g376)
    c: Block(g376)
    c: Distance(g376) = 450
    c: Block(g374)
    c: Block(g372)
    c: Block(g373)
    c: Block(g375)
FEATURE [Part::Extrusion] Extrude005
  Base = -> Sketch003
  Dir = (0,0,1)
  DirMode = 2
  FaceMakerClass = Part::FaceMakerBullseye
  LengthFwd = 24
  LengthRev = 0
  Solid = true
  Symmetric = false
